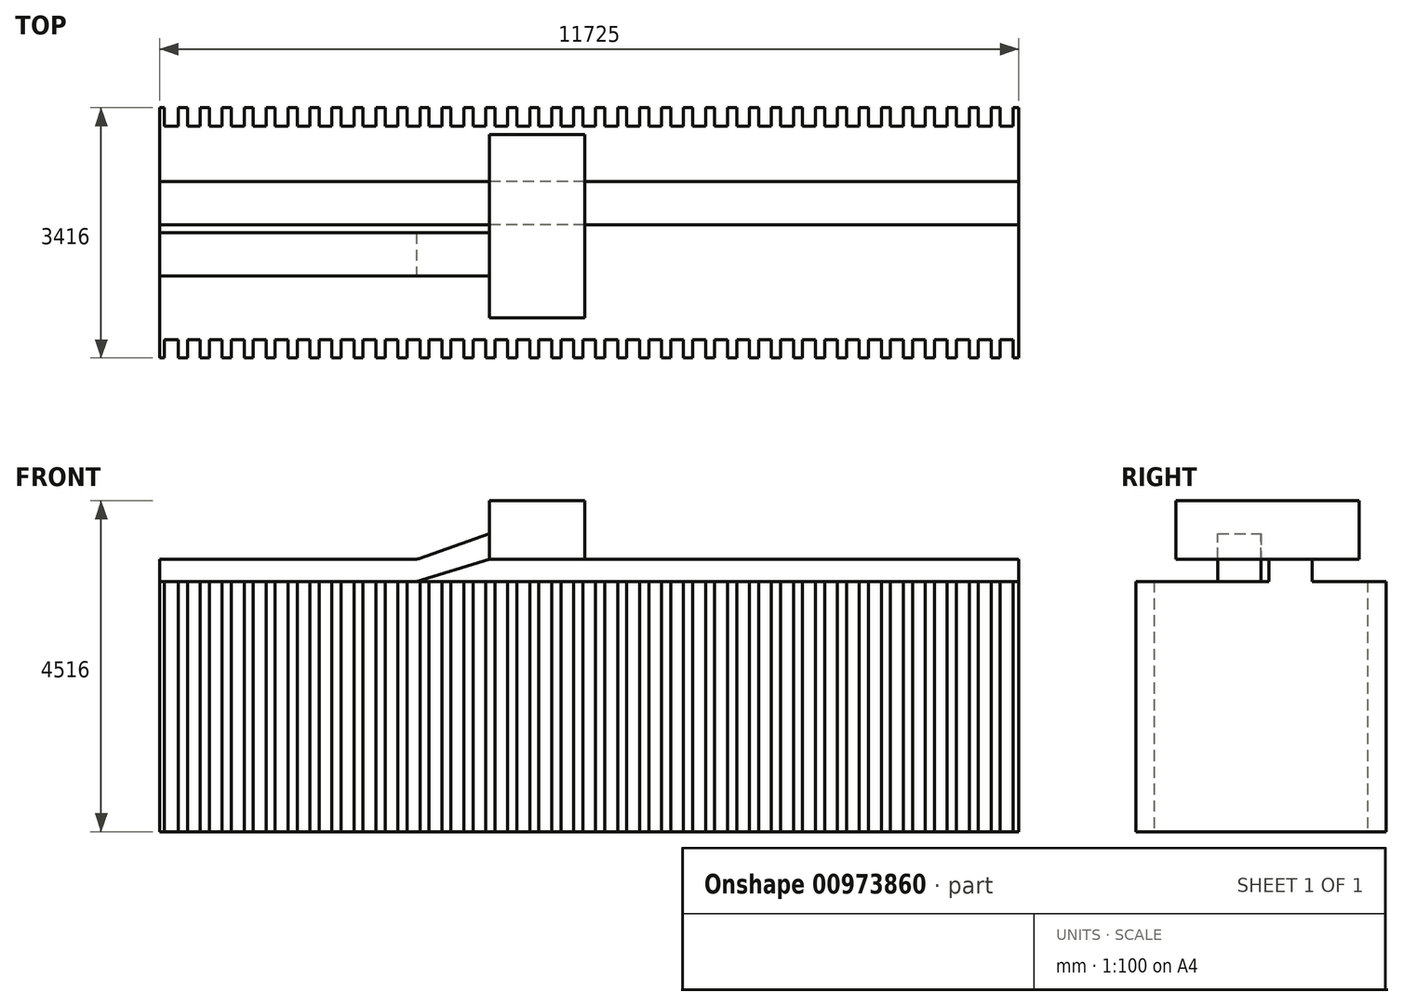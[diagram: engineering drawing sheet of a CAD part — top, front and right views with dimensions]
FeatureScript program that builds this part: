
annotation { "Feature Type Name" : "Feature", "Feature Type Description" : "" }
export const myFeature = defineFeature(function(context is Context, id is Id, definition is map)
    precondition{}
    {
        {
            var Q0;
            Q0=qCreatedBy(makeId("Top.planeOp"),FACE);
            var sketch = newSketch(context, id + "F0", { "sketchPlane" : qUnion([Q0])});
            skLineSegment(sketch, "E0.bottom", {"start": v(-25000, 7300) * mm, "end": v(25000, 7300) * mm});
            skLineSegment(sketch, "E0.top", {"start": v(-25000, -7300) * mm, "end": v(25000, -7300) * mm});
            skLineSegment(sketch, "E0.left", {"start": v(-25000, 7300) * mm, "end": v(-25000, -7300) * mm});
            skLineSegment(sketch, "E0.right", {"start": v(25000, 7300) * mm, "end": v(25000, -7300) * mm});
            skPoint(sketch, "E0.middle", {"position": v(0, 0) * mm});
            skSolve(sketch);
        }
        {
            var Q0;
            Q0=makeQuery(id+"F0.imprint","IMPRINT",FACE,{"disambiguationData":[TD([[makeQuery(id+"F0.imprint","IMPRINT",EDGE,{"derivedFrom":sQuery(id+"F0.wireOp",EDGE,"E0.bottom")}),-1.0]])]});
            var sketch = newSketch(context, id + "F1", { "sketchPlane" : qUnion([Q0])});
            skLineSegment(sketch, "E1", {"start": v(-20201.46, 5909) * mm, "end": v(-20138.96, 5909) * mm});
            skLineSegment(sketch, "E2", {"start": v(-20201.46, 5909) * mm, "end": v(-20201.46, 2493) * mm});
            skLineSegment(sketch, "E3", {"start": v(-20201.46, 2493) * mm, "end": v(-20138.96, 2493) * mm});
            skLineSegment(sketch, "E4", {"start": v(-8476.46, 2493) * mm, "end": v(-8476.46, 5909) * mm});
            skLineSegment(sketch, "E5.0", {"start": v(-20138.96, 5909) * mm, "end": v(-20138.96, 2493) * mm});
            skLineSegment(sketch, "E6.0", {"start": v(-19951.46, 5909) * mm, "end": v(-19951.46, 2493) * mm});
            skLineSegment(sketch, "E7.0", {"start": v(-19651.46, 5909) * mm, "end": v(-19651.46, 2493) * mm});
            skLineSegment(sketch, "E8.0", {"start": v(-19351.46, 5909) * mm, "end": v(-19351.46, 2493) * mm});
            skLineSegment(sketch, "E9.0", {"start": v(-19051.46, 5909) * mm, "end": v(-19051.46, 2493) * mm});
            skLineSegment(sketch, "E10.0", {"start": v(-18751.46, 5909) * mm, "end": v(-18751.46, 2493) * mm});
            skLineSegment(sketch, "E11.0", {"start": v(-18451.46, 5909) * mm, "end": v(-18451.46, 2493) * mm});
            skLineSegment(sketch, "E12.0", {"start": v(-18151.46, 5909) * mm, "end": v(-18151.46, 2493) * mm});
            skLineSegment(sketch, "E13.0", {"start": v(-17851.46, 5909) * mm, "end": v(-17851.46, 2493) * mm});
            skLineSegment(sketch, "E14.0", {"start": v(-17551.46, 5909) * mm, "end": v(-17551.46, 2493) * mm});
            skLineSegment(sketch, "E15.0", {"start": v(-17251.46, 5909) * mm, "end": v(-17251.46, 2493) * mm});
            skLineSegment(sketch, "E16.0", {"start": v(-16951.46, 5909) * mm, "end": v(-16951.46, 2493) * mm});
            skLineSegment(sketch, "E17.0", {"start": v(-16651.46, 5909) * mm, "end": v(-16651.46, 2493) * mm});
            skLineSegment(sketch, "E18.0", {"start": v(-16351.46, 5909) * mm, "end": v(-16351.46, 2493) * mm});
            skLineSegment(sketch, "E19.0", {"start": v(-16051.46, 5909) * mm, "end": v(-16051.46, 2493) * mm});
            skLineSegment(sketch, "E20.0", {"start": v(-15751.46, 5909) * mm, "end": v(-15751.46, 2493) * mm});
            skLineSegment(sketch, "E21.0", {"start": v(-25005, 7305) * mm, "end": v(-25005, -7305) * mm});
            skLineSegment(sketch, "E21.1", {"start": v(25005, 7305) * mm, "end": v(-25005, 7305) * mm});
            skLineSegment(sketch, "E21.2", {"start": v(25005, -7305) * mm, "end": v(25005, 7305) * mm});
            skLineSegment(sketch, "E21.3", {"start": v(-25005, -7305) * mm, "end": v(25005, -7305) * mm});
            skLineSegment(sketch, "E22.0", {"start": v(-15451.46, 5909) * mm, "end": v(-15451.46, 2493) * mm});
            skLineSegment(sketch, "E23.0", {"start": v(-15151.46, 5909) * mm, "end": v(-15151.46, 2493) * mm});
            skLineSegment(sketch, "E24.0", {"start": v(-14851.46, 5909) * mm, "end": v(-14851.46, 2493) * mm});
            skLineSegment(sketch, "E25.0", {"start": v(-14551.46, 5909) * mm, "end": v(-14551.46, 2493) * mm});
            skLineSegment(sketch, "E26.0", {"start": v(-14251.46, 5909) * mm, "end": v(-14251.46, 2493) * mm});
            skLineSegment(sketch, "E27.0", {"start": v(-13951.46, 5909) * mm, "end": v(-13951.46, 2493) * mm});
            skLineSegment(sketch, "E28.0", {"start": v(-13651.46, 5909) * mm, "end": v(-13651.46, 2493) * mm});
            skLineSegment(sketch, "E29.0", {"start": v(-13351.46, 5909) * mm, "end": v(-13351.46, 2493) * mm});
            skLineSegment(sketch, "E30.0", {"start": v(-13051.46, 5909) * mm, "end": v(-13051.46, 2493) * mm});
            skLineSegment(sketch, "E31.0", {"start": v(-12751.46, 5909) * mm, "end": v(-12751.46, 2493) * mm});
            skLineSegment(sketch, "E32.0", {"start": v(-12451.46, 5909) * mm, "end": v(-12451.46, 2493) * mm});
            skLineSegment(sketch, "E33.0", {"start": v(-12151.46, 5909) * mm, "end": v(-12151.46, 2493) * mm});
            skLineSegment(sketch, "E34.0", {"start": v(-11851.46, 5909) * mm, "end": v(-11851.46, 2493) * mm});
            skLineSegment(sketch, "E35.0", {"start": v(-11551.46, 5909) * mm, "end": v(-11551.46, 2493) * mm});
            skLineSegment(sketch, "E36.0", {"start": v(-11251.46, 5909) * mm, "end": v(-11251.46, 2493) * mm});
            skLineSegment(sketch, "E37.0", {"start": v(-10951.46, 5909) * mm, "end": v(-10951.46, 2493) * mm});
            skLineSegment(sketch, "E38.0", {"start": v(-10651.46, 5909) * mm, "end": v(-10651.46, 2493) * mm});
            skLineSegment(sketch, "E39.0", {"start": v(-10351.46, 5909) * mm, "end": v(-10351.46, 2493) * mm});
            skLineSegment(sketch, "E40.0", {"start": v(-10051.46, 5909) * mm, "end": v(-10051.46, 2493) * mm});
            skLineSegment(sketch, "E41.0", {"start": v(-9751.46, 5909) * mm, "end": v(-9751.46, 2493) * mm});
            skLineSegment(sketch, "E42.0", {"start": v(-9451.46, 5909) * mm, "end": v(-9451.46, 2493) * mm});
            skLineSegment(sketch, "E43.0", {"start": v(-9151.46, 5909) * mm, "end": v(-9151.46, 2493) * mm});
            skLineSegment(sketch, "E44.0", {"start": v(-8851.46, 5909) * mm, "end": v(-8851.46, 2493) * mm});
            skLineSegment(sketch, "E45.0", {"start": v(-8551.46, 5909) * mm, "end": v(-8551.46, 2493) * mm});
            skLineSegment(sketch, "E46.0", {"start": v(-19826.46, 5909) * mm, "end": v(-19826.46, 2493) * mm});
            skLineSegment(sketch, "E47.0", {"start": v(-19526.46, 5909) * mm, "end": v(-19526.46, 2493) * mm});
            skLineSegment(sketch, "E48.0", {"start": v(-19226.46, 5909) * mm, "end": v(-19226.46, 2493) * mm});
            skLineSegment(sketch, "E49.0", {"start": v(-18926.46, 5909) * mm, "end": v(-18926.46, 2493) * mm});
            skLineSegment(sketch, "E50.0", {"start": v(-18626.46, 5909) * mm, "end": v(-18626.46, 2493) * mm});
            skLineSegment(sketch, "E51.0", {"start": v(-18326.46, 5909) * mm, "end": v(-18326.46, 2493) * mm});
            skLineSegment(sketch, "E52.0", {"start": v(-18026.46, 5909) * mm, "end": v(-18026.46, 2493) * mm});
            skLineSegment(sketch, "E53.0", {"start": v(-17726.46, 5909) * mm, "end": v(-17726.46, 2493) * mm});
            skLineSegment(sketch, "E54.0", {"start": v(-17426.46, 5909) * mm, "end": v(-17426.46, 2493) * mm});
            skLineSegment(sketch, "E55.0", {"start": v(-17126.46, 5909) * mm, "end": v(-17126.46, 2493) * mm});
            skLineSegment(sketch, "E56.0", {"start": v(-16826.46, 5909) * mm, "end": v(-16826.46, 2493) * mm});
            skLineSegment(sketch, "E57.0", {"start": v(-16526.46, 5909) * mm, "end": v(-16526.46, 2493) * mm});
            skLineSegment(sketch, "E58.0", {"start": v(-16226.46, 5909) * mm, "end": v(-16226.46, 2493) * mm});
            skLineSegment(sketch, "E59.0", {"start": v(-15926.46, 5909) * mm, "end": v(-15926.46, 2493) * mm});
            skLineSegment(sketch, "E60.0", {"start": v(-15626.46, 5909) * mm, "end": v(-15626.46, 2493) * mm});
            skLineSegment(sketch, "E61.0", {"start": v(-15326.46, 5909) * mm, "end": v(-15326.46, 2493) * mm});
            skLineSegment(sketch, "E62.0", {"start": v(-15026.46, 5909) * mm, "end": v(-15026.46, 2493) * mm});
            skLineSegment(sketch, "E63.0", {"start": v(-14726.46, 5909) * mm, "end": v(-14726.46, 2493) * mm});
            skLineSegment(sketch, "E64.0", {"start": v(-14426.46, 5909) * mm, "end": v(-14426.46, 2493) * mm});
            skLineSegment(sketch, "E65.0", {"start": v(-14126.46, 5909) * mm, "end": v(-14126.46, 2493) * mm});
            skLineSegment(sketch, "E66.0", {"start": v(-13826.46, 5909) * mm, "end": v(-13826.46, 2493) * mm});
            skLineSegment(sketch, "E67.0", {"start": v(-13526.46, 5909) * mm, "end": v(-13526.46, 2493) * mm});
            skLineSegment(sketch, "E68.0", {"start": v(-13226.46, 5909) * mm, "end": v(-13226.46, 2493) * mm});
            skLineSegment(sketch, "E69.0", {"start": v(-12926.46, 5909) * mm, "end": v(-12926.46, 2493) * mm});
            skLineSegment(sketch, "E70.0", {"start": v(-12626.46, 5909) * mm, "end": v(-12626.46, 2493) * mm});
            skLineSegment(sketch, "E71.0", {"start": v(-12326.46, 5909) * mm, "end": v(-12326.46, 2493) * mm});
            skLineSegment(sketch, "E72.0", {"start": v(-12026.46, 5909) * mm, "end": v(-12026.46, 2493) * mm});
            skLineSegment(sketch, "E73.0", {"start": v(-11726.46, 5909) * mm, "end": v(-11726.46, 2493) * mm});
            skLineSegment(sketch, "E74.0", {"start": v(-11426.46, 5909) * mm, "end": v(-11426.46, 2493) * mm});
            skLineSegment(sketch, "E75.0", {"start": v(-11126.46, 5909) * mm, "end": v(-11126.46, 2493) * mm});
            skLineSegment(sketch, "E76.0", {"start": v(-10826.46, 5909) * mm, "end": v(-10826.46, 2493) * mm});
            skLineSegment(sketch, "E77.0", {"start": v(-10526.46, 5909) * mm, "end": v(-10526.46, 2493) * mm});
            skLineSegment(sketch, "E78.0", {"start": v(-10226.46, 5909) * mm, "end": v(-10226.46, 2493) * mm});
            skLineSegment(sketch, "E79.0", {"start": v(-9926.46, 5909) * mm, "end": v(-9926.46, 2493) * mm});
            skLineSegment(sketch, "E80.0", {"start": v(-9626.46, 5909) * mm, "end": v(-9626.46, 2493) * mm});
            skLineSegment(sketch, "E81.0", {"start": v(-9326.46, 5909) * mm, "end": v(-9326.46, 2493) * mm});
            skLineSegment(sketch, "E82.0", {"start": v(-9026.46, 5909) * mm, "end": v(-9026.46, 2493) * mm});
            skLineSegment(sketch, "E83.0", {"start": v(-8726.46, 5909) * mm, "end": v(-8726.46, 2493) * mm});
            skLineSegment(sketch, "E84", {"start": v(-20201.46, 5659) * mm, "end": v(-8476.46, 5659) * mm});
            skLineSegment(sketch, "E85", {"start": v(-20201.46, 2743) * mm, "end": v(-8476.46, 2743) * mm});
            skLineSegment(sketch, "E86.trimOffspring", {"start": v(-8551.46, 5909) * mm, "end": v(-8476.46, 5909) * mm});
            skLineSegment(sketch, "E87.trimOffspring", {"start": v(-8851.46, 5909) * mm, "end": v(-8726.46, 5909) * mm});
            skLineSegment(sketch, "E88.trimOffspring", {"start": v(-9151.46, 5909) * mm, "end": v(-9026.46, 5909) * mm});
            skLineSegment(sketch, "E89.trimOffspring", {"start": v(-9451.46, 5909) * mm, "end": v(-9326.46, 5909) * mm});
            skLineSegment(sketch, "E90.trimOffspring", {"start": v(-9751.46, 5909) * mm, "end": v(-9626.46, 5909) * mm});
            skLineSegment(sketch, "E91.trimOffspring", {"start": v(-10051.46, 5909) * mm, "end": v(-9926.46, 5909) * mm});
            skLineSegment(sketch, "E92.trimOffspring", {"start": v(-10351.46, 5909) * mm, "end": v(-10226.46, 5909) * mm});
            skLineSegment(sketch, "E93.trimOffspring", {"start": v(-10651.46, 5909) * mm, "end": v(-10526.46, 5909) * mm});
            skLineSegment(sketch, "E94.trimOffspring", {"start": v(-10951.46, 5909) * mm, "end": v(-10826.46, 5909) * mm});
            skLineSegment(sketch, "E95.trimOffspring", {"start": v(-11251.46, 5909) * mm, "end": v(-11126.46, 5909) * mm});
            skLineSegment(sketch, "E96.trimOffspring", {"start": v(-11551.46, 5909) * mm, "end": v(-11426.46, 5909) * mm});
            skLineSegment(sketch, "E97.trimOffspring", {"start": v(-11851.46, 5909) * mm, "end": v(-11726.46, 5909) * mm});
            skLineSegment(sketch, "E98.trimOffspring", {"start": v(-12151.46, 5909) * mm, "end": v(-12026.46, 5909) * mm});
            skLineSegment(sketch, "E99.trimOffspring", {"start": v(-12451.46, 5909) * mm, "end": v(-12326.46, 5909) * mm});
            skLineSegment(sketch, "E100.trimOffspring", {"start": v(-12751.46, 5909) * mm, "end": v(-12626.46, 5909) * mm});
            skLineSegment(sketch, "E101.trimOffspring", {"start": v(-13051.46, 5909) * mm, "end": v(-12926.46, 5909) * mm});
            skLineSegment(sketch, "E102.trimOffspring", {"start": v(-13351.46, 5909) * mm, "end": v(-13226.46, 5909) * mm});
            skLineSegment(sketch, "E103.trimOffspring", {"start": v(-13651.46, 5909) * mm, "end": v(-13526.46, 5909) * mm});
            skLineSegment(sketch, "E104.trimOffspring", {"start": v(-13951.46, 5909) * mm, "end": v(-13826.46, 5909) * mm});
            skLineSegment(sketch, "E105.trimOffspring", {"start": v(-14251.46, 5909) * mm, "end": v(-14126.46, 5909) * mm});
            skLineSegment(sketch, "E106.trimOffspring", {"start": v(-14551.46, 5909) * mm, "end": v(-14426.46, 5909) * mm});
            skLineSegment(sketch, "E107.trimOffspring", {"start": v(-14851.46, 5909) * mm, "end": v(-14726.46, 5909) * mm});
            skLineSegment(sketch, "E108.trimOffspring", {"start": v(-15151.46, 5909) * mm, "end": v(-15026.46, 5909) * mm});
            skLineSegment(sketch, "E109.trimOffspring", {"start": v(-15451.46, 5909) * mm, "end": v(-15326.46, 5909) * mm});
            skLineSegment(sketch, "E110.trimOffspring", {"start": v(-15751.46, 5909) * mm, "end": v(-15626.46, 5909) * mm});
            skLineSegment(sketch, "E111.trimOffspring", {"start": v(-16051.46, 5909) * mm, "end": v(-15926.46, 5909) * mm});
            skLineSegment(sketch, "E112.trimOffspring", {"start": v(-16351.46, 5909) * mm, "end": v(-16226.46, 5909) * mm});
            skLineSegment(sketch, "E113.trimOffspring", {"start": v(-16651.46, 5909) * mm, "end": v(-16526.46, 5909) * mm});
            skLineSegment(sketch, "E114.trimOffspring", {"start": v(-16951.46, 5909) * mm, "end": v(-16826.46, 5909) * mm});
            skLineSegment(sketch, "E115.trimOffspring", {"start": v(-17251.46, 5909) * mm, "end": v(-17126.46, 5909) * mm});
            skLineSegment(sketch, "E116.trimOffspring", {"start": v(-17551.46, 5909) * mm, "end": v(-17426.46, 5909) * mm});
            skLineSegment(sketch, "E117.trimOffspring", {"start": v(-17851.46, 5909) * mm, "end": v(-17726.46, 5909) * mm});
            skLineSegment(sketch, "E118.trimOffspring", {"start": v(-18151.46, 5909) * mm, "end": v(-18026.46, 5909) * mm});
            skLineSegment(sketch, "E119.trimOffspring", {"start": v(-18451.46, 5909) * mm, "end": v(-18326.46, 5909) * mm});
            skLineSegment(sketch, "E120.trimOffspring", {"start": v(-18751.46, 5909) * mm, "end": v(-18626.46, 5909) * mm});
            skLineSegment(sketch, "E121.trimOffspring", {"start": v(-19051.46, 5909) * mm, "end": v(-18926.46, 5909) * mm});
            skLineSegment(sketch, "E122.trimOffspring", {"start": v(-19351.46, 5909) * mm, "end": v(-19226.46, 5909) * mm});
            skLineSegment(sketch, "E123.trimOffspring", {"start": v(-19651.46, 5909) * mm, "end": v(-19526.46, 5909) * mm});
            skLineSegment(sketch, "E124.trimOffspring", {"start": v(-19951.46, 5909) * mm, "end": v(-19826.46, 5909) * mm});
            skLineSegment(sketch, "E125.trimOffspring", {"start": v(-19651.46, 2493) * mm, "end": v(-19526.46, 2493) * mm});
            skLineSegment(sketch, "E126.trimOffspring", {"start": v(-18751.46, 2493) * mm, "end": v(-18626.46, 2493) * mm});
            skLineSegment(sketch, "E127.trimOffspring", {"start": v(-17851.46, 2493) * mm, "end": v(-17726.46, 2493) * mm});
            skLineSegment(sketch, "E128.trimOffspring", {"start": v(-17251.46, 2493) * mm, "end": v(-17126.46, 2493) * mm});
            skLineSegment(sketch, "E129.trimOffspring", {"start": v(-16351.46, 2493) * mm, "end": v(-16226.46, 2493) * mm});
            skLineSegment(sketch, "E130.trimOffspring", {"start": v(-16951.46, 2493) * mm, "end": v(-16826.46, 2493) * mm});
            skLineSegment(sketch, "E131", {"start": v(-17551.46, 2493) * mm, "end": v(-17426.46, 2493) * mm});
            skLineSegment(sketch, "E132", {"start": v(-16651.46, 2493) * mm, "end": v(-16526.46, 2493) * mm});
            skLineSegment(sketch, "E133.trimOffspring", {"start": v(-15751.46, 2493) * mm, "end": v(-15626.46, 2493) * mm});
            skLineSegment(sketch, "E134.trimOffspring", {"start": v(-14551.46, 2493) * mm, "end": v(-14426.46, 2493) * mm});
            skLineSegment(sketch, "E135.trimOffspring", {"start": v(-15151.46, 2493) * mm, "end": v(-15026.46, 2493) * mm});
            skLineSegment(sketch, "E136.trimOffspring", {"start": v(-15451.46, 2493) * mm, "end": v(-15326.46, 2493) * mm});
            skLineSegment(sketch, "E137", {"start": v(-14851.46, 2493) * mm, "end": v(-14726.46, 2493) * mm});
            skLineSegment(sketch, "E138.trimOffspring", {"start": v(-13951.46, 2493) * mm, "end": v(-13826.46, 2493) * mm});
            skLineSegment(sketch, "E139.trimOffspring", {"start": v(-13351.46, 2493) * mm, "end": v(-13226.46, 2493) * mm});
            skLineSegment(sketch, "E140.trimOffspring", {"start": v(-13651.46, 2493) * mm, "end": v(-13526.46, 2493) * mm});
            skLineSegment(sketch, "E141", {"start": v(-14251.46, 2493) * mm, "end": v(-14126.46, 2493) * mm});
            skLineSegment(sketch, "E142.trimOffspring", {"start": v(-13051.46, 2493) * mm, "end": v(-12926.46, 2493) * mm});
            skLineSegment(sketch, "E143.trimOffspring", {"start": v(-12751.46, 2493) * mm, "end": v(-12626.46, 2493) * mm});
            skLineSegment(sketch, "E144.trimOffspring", {"start": v(-12151.46, 2493) * mm, "end": v(-12026.46, 2493) * mm});
            skLineSegment(sketch, "E145.trimOffspring", {"start": v(-11551.46, 2493) * mm, "end": v(-11426.46, 2493) * mm});
            skLineSegment(sketch, "E146.trimOffspring", {"start": v(-11851.46, 2493) * mm, "end": v(-11726.46, 2493) * mm});
            skLineSegment(sketch, "E147.trimOffspring", {"start": v(-11251.46, 2493) * mm, "end": v(-11126.46, 2493) * mm});
            skLineSegment(sketch, "E148.trimOffspring", {"start": v(-10951.46, 2493) * mm, "end": v(-10826.46, 2493) * mm});
            skLineSegment(sketch, "E149.trimOffspring", {"start": v(-10651.46, 2493) * mm, "end": v(-10526.46, 2493) * mm});
            skLineSegment(sketch, "E150.trimOffspring", {"start": v(-9751.46, 2493) * mm, "end": v(-9626.46, 2493) * mm});
            skLineSegment(sketch, "E151.trimOffspring", {"start": v(-8851.46, 2493) * mm, "end": v(-8726.46, 2493) * mm});
            skLineSegment(sketch, "E152", {"start": v(-10351.46, 2493) * mm, "end": v(-10226.46, 2493) * mm});
            skLineSegment(sketch, "E153", {"start": v(-10051.46, 2493) * mm, "end": v(-9926.46, 2493) * mm});
            skLineSegment(sketch, "E154", {"start": v(-9151.46, 2493) * mm, "end": v(-9026.46, 2493) * mm});
            skLineSegment(sketch, "E155.trimOffspring", {"start": v(-9451.46, 2493) * mm, "end": v(-9326.46, 2493) * mm});
            skLineSegment(sketch, "E156.trimOffspring", {"start": v(-8551.46, 2493) * mm, "end": v(-8476.46, 2493) * mm});
            skLineSegment(sketch, "E157.trimOffspring", {"start": v(-18451.46, 2493) * mm, "end": v(-18326.46, 2493) * mm});
            skLineSegment(sketch, "E158.trimOffspring", {"start": v(-19351.46, 2493) * mm, "end": v(-19226.46, 2493) * mm});
            skLineSegment(sketch, "E159", {"start": v(-19051.46, 2493) * mm, "end": v(-18926.46, 2493) * mm});
            skLineSegment(sketch, "E160", {"start": v(-18151.46, 2493) * mm, "end": v(-18026.46, 2493) * mm});
            skLineSegment(sketch, "E161", {"start": v(-16051.46, 2493) * mm, "end": v(-15926.46, 2493) * mm});
            skLineSegment(sketch, "E162", {"start": v(-19951.46, 2493) * mm, "end": v(-19826.46, 2493) * mm});
            skLineSegment(sketch, "E163", {"start": v(-12451.46, 2493) * mm, "end": v(-12326.46, 2493) * mm});
            skSolve(sketch);
        }
        {
            var Q0;
            {var subQ0=sQuery(id+"F1.wireOp",EDGE,"E88.trimOffspring");Q0=makeQuery(id+"F1.imprint","IMPRINT",FACE,{"disambiguationData":[TD([[makeQuery(id+"F1.imprint","IMPRINT",EDGE,{"derivedFrom":subQ0}),-1.0]])]});}
            var Q1;
            {var subQ0=sQuery(id+"F1.wireOp",EDGE,"E112.trimOffspring");Q1=makeQuery(id+"F1.imprint","IMPRINT",FACE,{"disambiguationData":[TD([[makeQuery(id+"F1.imprint","IMPRINT",EDGE,{"derivedFrom":subQ0}),-1.0]])]});}
            var Q2;
            {var subQ0=sQuery(id+"F1.wireOp",EDGE,"E84");var subQ1=sQuery(id+"F1.wireOp",EDGE,"E38.0");var subQ2=makeQuery(id+"F1.imprint","INTERSECT",VERTEX,{"derivedFrom":[subQ1,subQ0]});Q2=makeQuery(id+"F1.imprint","IMPRINT",FACE,{"disambiguationData":[TD([[makeQuery(id+"F1.imprint","IMPRINT",EDGE,{"disambiguationData":[TD([[subQ2,-1.0]])],"derivedFrom":subQ1}),1.0]])]});}
            var Q3;
            {var subQ0=sQuery(id+"F1.wireOp",EDGE,"E158.trimOffspring");Q3=makeQuery(id+"F1.imprint","IMPRINT",FACE,{"disambiguationData":[TD([[makeQuery(id+"F1.imprint","IMPRINT",EDGE,{"derivedFrom":subQ0}),1.0]])]});}
            var Q4;
            {var subQ0=sQuery(id+"F1.wireOp",EDGE,"E84");var subQ1=sQuery(id+"F1.wireOp",EDGE,"E18.0");var subQ2=makeQuery(id+"F1.imprint","INTERSECT",VERTEX,{"derivedFrom":[subQ1,subQ0]});Q4=makeQuery(id+"F1.imprint","IMPRINT",FACE,{"disambiguationData":[TD([[makeQuery(id+"F1.imprint","IMPRINT",EDGE,{"disambiguationData":[TD([[subQ2,-1.0]])],"derivedFrom":subQ1}),-1.0]])]});}
            var Q5;
            {var subQ0=sQuery(id+"F1.wireOp",EDGE,"E140.trimOffspring");Q5=makeQuery(id+"F1.imprint","IMPRINT",FACE,{"disambiguationData":[TD([[makeQuery(id+"F1.imprint","IMPRINT",EDGE,{"derivedFrom":subQ0}),1.0]])]});}
            var Q6;
            {var subQ0=sQuery(id+"F1.wireOp",EDGE,"E84");var subQ1=sQuery(id+"F1.wireOp",EDGE,"E35.0");var subQ2=makeQuery(id+"F1.imprint","INTERSECT",VERTEX,{"derivedFrom":[subQ1,subQ0]});Q6=makeQuery(id+"F1.imprint","IMPRINT",FACE,{"disambiguationData":[TD([[makeQuery(id+"F1.imprint","IMPRINT",EDGE,{"disambiguationData":[TD([[subQ2,-1.0]])],"derivedFrom":subQ1}),-1.0]])]});}
            var Q7;
            {var subQ0=sQuery(id+"F1.wireOp",EDGE,"E107.trimOffspring");Q7=makeQuery(id+"F1.imprint","IMPRINT",FACE,{"disambiguationData":[TD([[makeQuery(id+"F1.imprint","IMPRINT",EDGE,{"derivedFrom":subQ0}),-1.0]])]});}
            var Q8;
            {var subQ0=sQuery(id+"F1.wireOp",EDGE,"E129.trimOffspring");Q8=makeQuery(id+"F1.imprint","IMPRINT",FACE,{"disambiguationData":[TD([[makeQuery(id+"F1.imprint","IMPRINT",EDGE,{"derivedFrom":subQ0}),1.0]])]});}
            var Q9;
            {var subQ0=sQuery(id+"F1.wireOp",EDGE,"E120.trimOffspring");Q9=makeQuery(id+"F1.imprint","IMPRINT",FACE,{"disambiguationData":[TD([[makeQuery(id+"F1.imprint","IMPRINT",EDGE,{"derivedFrom":subQ0}),-1.0]])]});}
            var Q10;
            {var subQ0=sQuery(id+"F1.wireOp",EDGE,"E115.trimOffspring");Q10=makeQuery(id+"F1.imprint","IMPRINT",FACE,{"disambiguationData":[TD([[makeQuery(id+"F1.imprint","IMPRINT",EDGE,{"derivedFrom":subQ0}),-1.0]])]});}
            var Q11;
            {var subQ0=sQuery(id+"F1.wireOp",EDGE,"E138.trimOffspring");Q11=makeQuery(id+"F1.imprint","IMPRINT",FACE,{"disambiguationData":[TD([[makeQuery(id+"F1.imprint","IMPRINT",EDGE,{"derivedFrom":subQ0}),1.0]])]});}
            var Q12;
            {var subQ0=sQuery(id+"F1.wireOp",EDGE,"E84");var subQ1=sQuery(id+"F1.wireOp",EDGE,"E11.0");var subQ2=makeQuery(id+"F1.imprint","INTERSECT",VERTEX,{"derivedFrom":[subQ1,subQ0]});Q12=makeQuery(id+"F1.imprint","IMPRINT",FACE,{"disambiguationData":[TD([[makeQuery(id+"F1.imprint","IMPRINT",EDGE,{"disambiguationData":[TD([[subQ2,-1.0]])],"derivedFrom":subQ1}),1.0]])]});}
            var Q13;
            {var subQ0=sQuery(id+"F1.wireOp",EDGE,"E91.trimOffspring");Q13=makeQuery(id+"F1.imprint","IMPRINT",FACE,{"disambiguationData":[TD([[makeQuery(id+"F1.imprint","IMPRINT",EDGE,{"derivedFrom":subQ0}),-1.0]])]});}
            var Q14;
            {var subQ0=sQuery(id+"F1.wireOp",EDGE,"E84");var subQ1=sQuery(id+"F1.wireOp",EDGE,"E13.0");var subQ2=makeQuery(id+"F1.imprint","INTERSECT",VERTEX,{"derivedFrom":[subQ1,subQ0]});Q14=makeQuery(id+"F1.imprint","IMPRINT",FACE,{"disambiguationData":[TD([[makeQuery(id+"F1.imprint","IMPRINT",EDGE,{"disambiguationData":[TD([[subQ2,-1.0]])],"derivedFrom":subQ1}),-1.0]])]});}
            var Q15;
            {var subQ0=sQuery(id+"F1.wireOp",EDGE,"E84");var subQ1=sQuery(id+"F1.wireOp",EDGE,"E26.0");var subQ2=makeQuery(id+"F1.imprint","INTERSECT",VERTEX,{"derivedFrom":[subQ1,subQ0]});Q15=makeQuery(id+"F1.imprint","IMPRINT",FACE,{"disambiguationData":[TD([[makeQuery(id+"F1.imprint","IMPRINT",EDGE,{"disambiguationData":[TD([[subQ2,-1.0]])],"derivedFrom":subQ1}),-1.0]])]});}
            var Q16;
            {var subQ0=sQuery(id+"F1.wireOp",EDGE,"E121.trimOffspring");Q16=makeQuery(id+"F1.imprint","IMPRINT",FACE,{"disambiguationData":[TD([[makeQuery(id+"F1.imprint","IMPRINT",EDGE,{"derivedFrom":subQ0}),-1.0]])]});}
            var Q17;
            {var subQ0=sQuery(id+"F1.wireOp",EDGE,"E130.trimOffspring");Q17=makeQuery(id+"F1.imprint","IMPRINT",FACE,{"disambiguationData":[TD([[makeQuery(id+"F1.imprint","IMPRINT",EDGE,{"derivedFrom":subQ0}),1.0]])]});}
            var Q18;
            {var subQ0=sQuery(id+"F1.wireOp",EDGE,"E154");Q18=makeQuery(id+"F1.imprint","IMPRINT",FACE,{"disambiguationData":[TD([[makeQuery(id+"F1.imprint","IMPRINT",EDGE,{"derivedFrom":subQ0}),1.0]])]});}
            var Q19;
            {var subQ0=sQuery(id+"F1.wireOp",EDGE,"E151.trimOffspring");Q19=makeQuery(id+"F1.imprint","IMPRINT",FACE,{"disambiguationData":[TD([[makeQuery(id+"F1.imprint","IMPRINT",EDGE,{"derivedFrom":subQ0}),1.0]])]});}
            var Q20;
            {var subQ0=sQuery(id+"F1.wireOp",EDGE,"E84");var subQ1=sQuery(id+"F1.wireOp",EDGE,"E30.0");var subQ2=makeQuery(id+"F1.imprint","INTERSECT",VERTEX,{"derivedFrom":[subQ1,subQ0]});Q20=makeQuery(id+"F1.imprint","IMPRINT",FACE,{"disambiguationData":[TD([[makeQuery(id+"F1.imprint","IMPRINT",EDGE,{"disambiguationData":[TD([[subQ2,-1.0]])],"derivedFrom":subQ1}),-1.0]])]});}
            var Q21;
            {var subQ0=sQuery(id+"F1.wireOp",EDGE,"E84");var subQ1=sQuery(id+"F1.wireOp",EDGE,"E19.0");var subQ2=makeQuery(id+"F1.imprint","INTERSECT",VERTEX,{"derivedFrom":[subQ1,subQ0]});Q21=makeQuery(id+"F1.imprint","IMPRINT",FACE,{"disambiguationData":[TD([[makeQuery(id+"F1.imprint","IMPRINT",EDGE,{"disambiguationData":[TD([[subQ2,-1.0]])],"derivedFrom":subQ1}),1.0]])]});}
            var Q22;
            {var subQ0=sQuery(id+"F1.wireOp",EDGE,"E84");var subQ1=sQuery(id+"F1.wireOp",EDGE,"E14.0");var subQ2=makeQuery(id+"F1.imprint","INTERSECT",VERTEX,{"derivedFrom":[subQ1,subQ0]});Q22=makeQuery(id+"F1.imprint","IMPRINT",FACE,{"disambiguationData":[TD([[makeQuery(id+"F1.imprint","IMPRINT",EDGE,{"disambiguationData":[TD([[subQ2,-1.0]])],"derivedFrom":subQ1}),-1.0]])]});}
            var Q23;
            {var subQ0=sQuery(id+"F1.wireOp",EDGE,"E84");var subQ1=sQuery(id+"F1.wireOp",EDGE,"E12.0");var subQ2=makeQuery(id+"F1.imprint","INTERSECT",VERTEX,{"derivedFrom":[subQ1,subQ0]});Q23=makeQuery(id+"F1.imprint","IMPRINT",FACE,{"disambiguationData":[TD([[makeQuery(id+"F1.imprint","IMPRINT",EDGE,{"disambiguationData":[TD([[subQ2,-1.0]])],"derivedFrom":subQ1}),1.0]])]});}
            var Q24;
            {var subQ0=sQuery(id+"F1.wireOp",EDGE,"E143.trimOffspring");Q24=makeQuery(id+"F1.imprint","IMPRINT",FACE,{"disambiguationData":[TD([[makeQuery(id+"F1.imprint","IMPRINT",EDGE,{"derivedFrom":subQ0}),1.0]])]});}
            var Q25;
            {var subQ0=sQuery(id+"F1.wireOp",EDGE,"E161");Q25=makeQuery(id+"F1.imprint","IMPRINT",FACE,{"disambiguationData":[TD([[makeQuery(id+"F1.imprint","IMPRINT",EDGE,{"derivedFrom":subQ0}),1.0]])]});}
            var Q26;
            {var subQ0=sQuery(id+"F1.wireOp",EDGE,"E100.trimOffspring");Q26=makeQuery(id+"F1.imprint","IMPRINT",FACE,{"disambiguationData":[TD([[makeQuery(id+"F1.imprint","IMPRINT",EDGE,{"derivedFrom":subQ0}),-1.0]])]});}
            var Q27;
            {var subQ0=sQuery(id+"F1.wireOp",EDGE,"E84");var subQ1=sQuery(id+"F1.wireOp",EDGE,"E15.0");var subQ2=makeQuery(id+"F1.imprint","INTERSECT",VERTEX,{"derivedFrom":[subQ1,subQ0]});Q27=makeQuery(id+"F1.imprint","IMPRINT",FACE,{"disambiguationData":[TD([[makeQuery(id+"F1.imprint","IMPRINT",EDGE,{"disambiguationData":[TD([[subQ2,-1.0]])],"derivedFrom":subQ1}),-1.0]])]});}
            var Q28;
            {var subQ0=sQuery(id+"F1.wireOp",EDGE,"E84");var subQ1=sQuery(id+"F1.wireOp",EDGE,"E39.0");var subQ2=makeQuery(id+"F1.imprint","INTERSECT",VERTEX,{"derivedFrom":[subQ1,subQ0]});Q28=makeQuery(id+"F1.imprint","IMPRINT",FACE,{"disambiguationData":[TD([[makeQuery(id+"F1.imprint","IMPRINT",EDGE,{"disambiguationData":[TD([[subQ2,-1.0]])],"derivedFrom":subQ1}),1.0]])]});}
            var Q29;
            {var subQ0=sQuery(id+"F1.wireOp",EDGE,"E84");var subQ1=sQuery(id+"F1.wireOp",EDGE,"E36.0");var subQ2=makeQuery(id+"F1.imprint","INTERSECT",VERTEX,{"derivedFrom":[subQ1,subQ0]});Q29=makeQuery(id+"F1.imprint","IMPRINT",FACE,{"disambiguationData":[TD([[makeQuery(id+"F1.imprint","IMPRINT",EDGE,{"disambiguationData":[TD([[subQ2,-1.0]])],"derivedFrom":subQ1}),1.0]])]});}
            var Q30;
            {var subQ0=sQuery(id+"F1.wireOp",EDGE,"E84");var subQ1=sQuery(id+"F1.wireOp",EDGE,"E40.0");var subQ2=makeQuery(id+"F1.imprint","INTERSECT",VERTEX,{"derivedFrom":[subQ1,subQ0]});Q30=makeQuery(id+"F1.imprint","IMPRINT",FACE,{"disambiguationData":[TD([[makeQuery(id+"F1.imprint","IMPRINT",EDGE,{"disambiguationData":[TD([[subQ2,-1.0]])],"derivedFrom":subQ1}),1.0]])]});}
            var Q31;
            {var subQ0=sQuery(id+"F1.wireOp",EDGE,"E118.trimOffspring");Q31=makeQuery(id+"F1.imprint","IMPRINT",FACE,{"disambiguationData":[TD([[makeQuery(id+"F1.imprint","IMPRINT",EDGE,{"derivedFrom":subQ0}),-1.0]])]});}
            var Q32;
            {var subQ0=sQuery(id+"F1.wireOp",EDGE,"E84");var subQ1=sQuery(id+"F1.wireOp",EDGE,"E10.0");var subQ2=makeQuery(id+"F1.imprint","INTERSECT",VERTEX,{"derivedFrom":[subQ1,subQ0]});Q32=makeQuery(id+"F1.imprint","IMPRINT",FACE,{"disambiguationData":[TD([[makeQuery(id+"F1.imprint","IMPRINT",EDGE,{"disambiguationData":[TD([[subQ2,-1.0]])],"derivedFrom":subQ1}),-1.0]])]});}
            var Q33;
            {var subQ0=sQuery(id+"F1.wireOp",EDGE,"E84");var subQ1=sQuery(id+"F1.wireOp",EDGE,"E19.0");var subQ2=makeQuery(id+"F1.imprint","INTERSECT",VERTEX,{"derivedFrom":[subQ1,subQ0]});Q33=makeQuery(id+"F1.imprint","IMPRINT",FACE,{"disambiguationData":[TD([[makeQuery(id+"F1.imprint","IMPRINT",EDGE,{"disambiguationData":[TD([[subQ2,-1.0]])],"derivedFrom":subQ1}),-1.0]])]});}
            var Q34;
            {var subQ0=sQuery(id+"F1.wireOp",EDGE,"E84");var subQ1=sQuery(id+"F1.wireOp",EDGE,"E29.0");var subQ2=makeQuery(id+"F1.imprint","INTERSECT",VERTEX,{"derivedFrom":[subQ1,subQ0]});Q34=makeQuery(id+"F1.imprint","IMPRINT",FACE,{"disambiguationData":[TD([[makeQuery(id+"F1.imprint","IMPRINT",EDGE,{"disambiguationData":[TD([[subQ2,-1.0]])],"derivedFrom":subQ1}),-1.0]])]});}
            var Q35;
            {var subQ0=sQuery(id+"F1.wireOp",EDGE,"E84");var subQ1=sQuery(id+"F1.wireOp",EDGE,"E9.0");var subQ2=makeQuery(id+"F1.imprint","INTERSECT",VERTEX,{"derivedFrom":[subQ1,subQ0]});Q35=makeQuery(id+"F1.imprint","IMPRINT",FACE,{"disambiguationData":[TD([[makeQuery(id+"F1.imprint","IMPRINT",EDGE,{"disambiguationData":[TD([[subQ2,-1.0]])],"derivedFrom":subQ1}),-1.0]])]});}
            var Q36;
            {var subQ0=sQuery(id+"F1.wireOp",EDGE,"E102.trimOffspring");Q36=makeQuery(id+"F1.imprint","IMPRINT",FACE,{"disambiguationData":[TD([[makeQuery(id+"F1.imprint","IMPRINT",EDGE,{"derivedFrom":subQ0}),-1.0]])]});}
            var Q37;
            {var subQ0=sQuery(id+"F1.wireOp",EDGE,"E99.trimOffspring");Q37=makeQuery(id+"F1.imprint","IMPRINT",FACE,{"disambiguationData":[TD([[makeQuery(id+"F1.imprint","IMPRINT",EDGE,{"derivedFrom":subQ0}),-1.0]])]});}
            var Q38;
            {var subQ0=sQuery(id+"F1.wireOp",EDGE,"E117.trimOffspring");Q38=makeQuery(id+"F1.imprint","IMPRINT",FACE,{"disambiguationData":[TD([[makeQuery(id+"F1.imprint","IMPRINT",EDGE,{"derivedFrom":subQ0}),-1.0]])]});}
            var Q39;
            {var subQ0=sQuery(id+"F1.wireOp",EDGE,"E84");var subQ1=sQuery(id+"F1.wireOp",EDGE,"E17.0");var subQ2=makeQuery(id+"F1.imprint","INTERSECT",VERTEX,{"derivedFrom":[subQ1,subQ0]});Q39=makeQuery(id+"F1.imprint","IMPRINT",FACE,{"disambiguationData":[TD([[makeQuery(id+"F1.imprint","IMPRINT",EDGE,{"disambiguationData":[TD([[subQ2,-1.0]])],"derivedFrom":subQ1}),-1.0]])]});}
            var Q40;
            {var subQ0=sQuery(id+"F1.wireOp",EDGE,"E84");var subQ1=sQuery(id+"F1.wireOp",EDGE,"E33.0");var subQ2=makeQuery(id+"F1.imprint","INTERSECT",VERTEX,{"derivedFrom":[subQ1,subQ0]});Q40=makeQuery(id+"F1.imprint","IMPRINT",FACE,{"disambiguationData":[TD([[makeQuery(id+"F1.imprint","IMPRINT",EDGE,{"disambiguationData":[TD([[subQ2,-1.0]])],"derivedFrom":subQ1}),-1.0]])]});}
            var Q41;
            {var subQ0=sQuery(id+"F1.wireOp",EDGE,"E146.trimOffspring");Q41=makeQuery(id+"F1.imprint","IMPRINT",FACE,{"disambiguationData":[TD([[makeQuery(id+"F1.imprint","IMPRINT",EDGE,{"derivedFrom":subQ0}),1.0]])]});}
            var Q42;
            {var subQ0=sQuery(id+"F1.wireOp",EDGE,"E95.trimOffspring");Q42=makeQuery(id+"F1.imprint","IMPRINT",FACE,{"disambiguationData":[TD([[makeQuery(id+"F1.imprint","IMPRINT",EDGE,{"derivedFrom":subQ0}),-1.0]])]});}
            var Q43;
            {var subQ0=sQuery(id+"F1.wireOp",EDGE,"E134.trimOffspring");Q43=makeQuery(id+"F1.imprint","IMPRINT",FACE,{"disambiguationData":[TD([[makeQuery(id+"F1.imprint","IMPRINT",EDGE,{"derivedFrom":subQ0}),1.0]])]});}
            var Q44;
            {var subQ0=sQuery(id+"F1.wireOp",EDGE,"E122.trimOffspring");Q44=makeQuery(id+"F1.imprint","IMPRINT",FACE,{"disambiguationData":[TD([[makeQuery(id+"F1.imprint","IMPRINT",EDGE,{"derivedFrom":subQ0}),-1.0]])]});}
            var Q45;
            {var subQ0=sQuery(id+"F1.wireOp",EDGE,"E105.trimOffspring");Q45=makeQuery(id+"F1.imprint","IMPRINT",FACE,{"disambiguationData":[TD([[makeQuery(id+"F1.imprint","IMPRINT",EDGE,{"derivedFrom":subQ0}),-1.0]])]});}
            var Q46;
            {var subQ0=sQuery(id+"F1.wireOp",EDGE,"E84");var subQ1=sQuery(id+"F1.wireOp",EDGE,"E31.0");var subQ2=makeQuery(id+"F1.imprint","INTERSECT",VERTEX,{"derivedFrom":[subQ1,subQ0]});Q46=makeQuery(id+"F1.imprint","IMPRINT",FACE,{"disambiguationData":[TD([[makeQuery(id+"F1.imprint","IMPRINT",EDGE,{"disambiguationData":[TD([[subQ2,-1.0]])],"derivedFrom":subQ1}),-1.0]])]});}
            var Q47;
            {var subQ0=sQuery(id+"F1.wireOp",EDGE,"E84");var subQ1=sQuery(id+"F1.wireOp",EDGE,"E24.0");var subQ2=makeQuery(id+"F1.imprint","INTERSECT",VERTEX,{"derivedFrom":[subQ1,subQ0]});Q47=makeQuery(id+"F1.imprint","IMPRINT",FACE,{"disambiguationData":[TD([[makeQuery(id+"F1.imprint","IMPRINT",EDGE,{"disambiguationData":[TD([[subQ2,-1.0]])],"derivedFrom":subQ1}),1.0]])]});}
            var Q48;
            {var subQ0=sQuery(id+"F1.wireOp",EDGE,"E84");var subQ1=sQuery(id+"F1.wireOp",EDGE,"E43.0");var subQ2=makeQuery(id+"F1.imprint","INTERSECT",VERTEX,{"derivedFrom":[subQ1,subQ0]});Q48=makeQuery(id+"F1.imprint","IMPRINT",FACE,{"disambiguationData":[TD([[makeQuery(id+"F1.imprint","IMPRINT",EDGE,{"disambiguationData":[TD([[subQ2,-1.0]])],"derivedFrom":subQ1}),1.0]])]});}
            var Q49;
            {var subQ0=sQuery(id+"F1.wireOp",EDGE,"E123.trimOffspring");Q49=makeQuery(id+"F1.imprint","IMPRINT",FACE,{"disambiguationData":[TD([[makeQuery(id+"F1.imprint","IMPRINT",EDGE,{"derivedFrom":subQ0}),-1.0]])]});}
            var Q50;
            {var subQ0=sQuery(id+"F1.wireOp",EDGE,"E84");var subQ1=sQuery(id+"F1.wireOp",EDGE,"E43.0");var subQ2=makeQuery(id+"F1.imprint","INTERSECT",VERTEX,{"derivedFrom":[subQ1,subQ0]});Q50=makeQuery(id+"F1.imprint","IMPRINT",FACE,{"disambiguationData":[TD([[makeQuery(id+"F1.imprint","IMPRINT",EDGE,{"disambiguationData":[TD([[subQ2,-1.0]])],"derivedFrom":subQ1}),-1.0]])]});}
            var Q51;
            {var subQ0=sQuery(id+"F1.wireOp",EDGE,"E84");var subQ1=sQuery(id+"F1.wireOp",EDGE,"E32.0");var subQ2=makeQuery(id+"F1.imprint","INTERSECT",VERTEX,{"derivedFrom":[subQ1,subQ0]});Q51=makeQuery(id+"F1.imprint","IMPRINT",FACE,{"disambiguationData":[TD([[makeQuery(id+"F1.imprint","IMPRINT",EDGE,{"disambiguationData":[TD([[subQ2,-1.0]])],"derivedFrom":subQ1}),1.0]])]});}
            var Q52;
            {var subQ0=sQuery(id+"F1.wireOp",EDGE,"E133.trimOffspring");Q52=makeQuery(id+"F1.imprint","IMPRINT",FACE,{"disambiguationData":[TD([[makeQuery(id+"F1.imprint","IMPRINT",EDGE,{"derivedFrom":subQ0}),1.0]])]});}
            var Q53;
            {var subQ0=sQuery(id+"F1.wireOp",EDGE,"E84");var subQ1=sQuery(id+"F1.wireOp",EDGE,"E37.0");var subQ2=makeQuery(id+"F1.imprint","INTERSECT",VERTEX,{"derivedFrom":[subQ1,subQ0]});Q53=makeQuery(id+"F1.imprint","IMPRINT",FACE,{"disambiguationData":[TD([[makeQuery(id+"F1.imprint","IMPRINT",EDGE,{"disambiguationData":[TD([[subQ2,-1.0]])],"derivedFrom":subQ1}),1.0]])]});}
            var Q54;
            {var subQ0=sQuery(id+"F1.wireOp",EDGE,"E141");Q54=makeQuery(id+"F1.imprint","IMPRINT",FACE,{"disambiguationData":[TD([[makeQuery(id+"F1.imprint","IMPRINT",EDGE,{"derivedFrom":subQ0}),1.0]])]});}
            var Q55;
            {var subQ0=sQuery(id+"F1.wireOp",EDGE,"E84");var subQ1=sQuery(id+"F1.wireOp",EDGE,"E17.0");var subQ2=makeQuery(id+"F1.imprint","INTERSECT",VERTEX,{"derivedFrom":[subQ1,subQ0]});Q55=makeQuery(id+"F1.imprint","IMPRINT",FACE,{"disambiguationData":[TD([[makeQuery(id+"F1.imprint","IMPRINT",EDGE,{"disambiguationData":[TD([[subQ2,-1.0]])],"derivedFrom":subQ1}),1.0]])]});}
            var Q56;
            {var subQ0=sQuery(id+"F1.wireOp",EDGE,"E127.trimOffspring");Q56=makeQuery(id+"F1.imprint","IMPRINT",FACE,{"disambiguationData":[TD([[makeQuery(id+"F1.imprint","IMPRINT",EDGE,{"derivedFrom":subQ0}),1.0]])]});}
            var Q57;
            {var subQ0=sQuery(id+"F1.wireOp",EDGE,"E84");var subQ1=sQuery(id+"F1.wireOp",EDGE,"E8.0");var subQ2=makeQuery(id+"F1.imprint","INTERSECT",VERTEX,{"derivedFrom":[subQ1,subQ0]});Q57=makeQuery(id+"F1.imprint","IMPRINT",FACE,{"disambiguationData":[TD([[makeQuery(id+"F1.imprint","IMPRINT",EDGE,{"disambiguationData":[TD([[subQ2,-1.0]])],"derivedFrom":subQ1}),-1.0]])]});}
            var Q58;
            {var subQ0=sQuery(id+"F1.wireOp",EDGE,"E84");var subQ1=sQuery(id+"F1.wireOp",EDGE,"E35.0");var subQ2=makeQuery(id+"F1.imprint","INTERSECT",VERTEX,{"derivedFrom":[subQ1,subQ0]});Q58=makeQuery(id+"F1.imprint","IMPRINT",FACE,{"disambiguationData":[TD([[makeQuery(id+"F1.imprint","IMPRINT",EDGE,{"disambiguationData":[TD([[subQ2,-1.0]])],"derivedFrom":subQ1}),1.0]])]});}
            var Q59;
            {var subQ0=sQuery(id+"F1.wireOp",EDGE,"E84");var subQ1=sQuery(id+"F1.wireOp",EDGE,"E27.0");var subQ2=makeQuery(id+"F1.imprint","INTERSECT",VERTEX,{"derivedFrom":[subQ1,subQ0]});Q59=makeQuery(id+"F1.imprint","IMPRINT",FACE,{"disambiguationData":[TD([[makeQuery(id+"F1.imprint","IMPRINT",EDGE,{"disambiguationData":[TD([[subQ2,-1.0]])],"derivedFrom":subQ1}),1.0]])]});}
            var Q60;
            {var subQ0=sQuery(id+"F1.wireOp",EDGE,"E84");var subQ1=sQuery(id+"F1.wireOp",EDGE,"E42.0");var subQ2=makeQuery(id+"F1.imprint","INTERSECT",VERTEX,{"derivedFrom":[subQ1,subQ0]});Q60=makeQuery(id+"F1.imprint","IMPRINT",FACE,{"disambiguationData":[TD([[makeQuery(id+"F1.imprint","IMPRINT",EDGE,{"disambiguationData":[TD([[subQ2,-1.0]])],"derivedFrom":subQ1}),-1.0]])]});}
            var Q61;
            {var subQ0=sQuery(id+"F1.wireOp",EDGE,"E93.trimOffspring");Q61=makeQuery(id+"F1.imprint","IMPRINT",FACE,{"disambiguationData":[TD([[makeQuery(id+"F1.imprint","IMPRINT",EDGE,{"derivedFrom":subQ0}),-1.0]])]});}
            var Q62;
            {var subQ0=sQuery(id+"F1.wireOp",EDGE,"E84");var subQ1=sQuery(id+"F1.wireOp",EDGE,"E28.0");var subQ2=makeQuery(id+"F1.imprint","INTERSECT",VERTEX,{"derivedFrom":[subQ1,subQ0]});Q62=makeQuery(id+"F1.imprint","IMPRINT",FACE,{"disambiguationData":[TD([[makeQuery(id+"F1.imprint","IMPRINT",EDGE,{"disambiguationData":[TD([[subQ2,-1.0]])],"derivedFrom":subQ1}),-1.0]])]});}
            var Q63;
            {var subQ0=sQuery(id+"F1.wireOp",EDGE,"E84");var subQ1=sQuery(id+"F1.wireOp",EDGE,"E12.0");var subQ2=makeQuery(id+"F1.imprint","INTERSECT",VERTEX,{"derivedFrom":[subQ1,subQ0]});Q63=makeQuery(id+"F1.imprint","IMPRINT",FACE,{"disambiguationData":[TD([[makeQuery(id+"F1.imprint","IMPRINT",EDGE,{"disambiguationData":[TD([[subQ2,-1.0]])],"derivedFrom":subQ1}),-1.0]])]});}
            var Q64;
            {var subQ0=sQuery(id+"F1.wireOp",EDGE,"E84");var subQ1=sQuery(id+"F1.wireOp",EDGE,"E26.0");var subQ2=makeQuery(id+"F1.imprint","INTERSECT",VERTEX,{"derivedFrom":[subQ1,subQ0]});Q64=makeQuery(id+"F1.imprint","IMPRINT",FACE,{"disambiguationData":[TD([[makeQuery(id+"F1.imprint","IMPRINT",EDGE,{"disambiguationData":[TD([[subQ2,-1.0]])],"derivedFrom":subQ1}),1.0]])]});}
            var Q65;
            {var subQ0=sQuery(id+"F1.wireOp",EDGE,"E148.trimOffspring");Q65=makeQuery(id+"F1.imprint","IMPRINT",FACE,{"disambiguationData":[TD([[makeQuery(id+"F1.imprint","IMPRINT",EDGE,{"derivedFrom":subQ0}),1.0]])]});}
            var Q66;
            {var subQ0=sQuery(id+"F1.wireOp",EDGE,"E142.trimOffspring");Q66=makeQuery(id+"F1.imprint","IMPRINT",FACE,{"disambiguationData":[TD([[makeQuery(id+"F1.imprint","IMPRINT",EDGE,{"derivedFrom":subQ0}),1.0]])]});}
            var Q67;
            {var subQ0=sQuery(id+"F1.wireOp",EDGE,"E106.trimOffspring");Q67=makeQuery(id+"F1.imprint","IMPRINT",FACE,{"disambiguationData":[TD([[makeQuery(id+"F1.imprint","IMPRINT",EDGE,{"derivedFrom":subQ0}),-1.0]])]});}
            var Q68;
            {var subQ0=sQuery(id+"F1.wireOp",EDGE,"E84");var subQ1=sQuery(id+"F1.wireOp",EDGE,"E28.0");var subQ2=makeQuery(id+"F1.imprint","INTERSECT",VERTEX,{"derivedFrom":[subQ1,subQ0]});Q68=makeQuery(id+"F1.imprint","IMPRINT",FACE,{"disambiguationData":[TD([[makeQuery(id+"F1.imprint","IMPRINT",EDGE,{"disambiguationData":[TD([[subQ2,-1.0]])],"derivedFrom":subQ1}),1.0]])]});}
            var Q69;
            {var subQ0=sQuery(id+"F1.wireOp",EDGE,"E92.trimOffspring");Q69=makeQuery(id+"F1.imprint","IMPRINT",FACE,{"disambiguationData":[TD([[makeQuery(id+"F1.imprint","IMPRINT",EDGE,{"derivedFrom":subQ0}),-1.0]])]});}
            var Q70;
            {var subQ0=sQuery(id+"F1.wireOp",EDGE,"E84");var subQ1=sQuery(id+"F1.wireOp",EDGE,"E7.0");var subQ2=makeQuery(id+"F1.imprint","INTERSECT",VERTEX,{"derivedFrom":[subQ1,subQ0]});Q70=makeQuery(id+"F1.imprint","IMPRINT",FACE,{"disambiguationData":[TD([[makeQuery(id+"F1.imprint","IMPRINT",EDGE,{"disambiguationData":[TD([[subQ2,-1.0]])],"derivedFrom":subQ1}),-1.0]])]});}
            var Q71;
            {var subQ0=sQuery(id+"F1.wireOp",EDGE,"E84");var subQ1=sQuery(id+"F1.wireOp",EDGE,"E31.0");var subQ2=makeQuery(id+"F1.imprint","INTERSECT",VERTEX,{"derivedFrom":[subQ1,subQ0]});Q71=makeQuery(id+"F1.imprint","IMPRINT",FACE,{"disambiguationData":[TD([[makeQuery(id+"F1.imprint","IMPRINT",EDGE,{"disambiguationData":[TD([[subQ2,-1.0]])],"derivedFrom":subQ1}),1.0]])]});}
            var Q72;
            {var subQ0=sQuery(id+"F1.wireOp",EDGE,"E152");Q72=makeQuery(id+"F1.imprint","IMPRINT",FACE,{"disambiguationData":[TD([[makeQuery(id+"F1.imprint","IMPRINT",EDGE,{"derivedFrom":subQ0}),1.0]])]});}
            var Q73;
            {var subQ0=sQuery(id+"F1.wireOp",EDGE,"E87.trimOffspring");Q73=makeQuery(id+"F1.imprint","IMPRINT",FACE,{"disambiguationData":[TD([[makeQuery(id+"F1.imprint","IMPRINT",EDGE,{"derivedFrom":subQ0}),-1.0]])]});}
            var Q74;
            {var subQ0=sQuery(id+"F1.wireOp",EDGE,"E84");var subQ1=sQuery(id+"F1.wireOp",EDGE,"E22.0");var subQ2=makeQuery(id+"F1.imprint","INTERSECT",VERTEX,{"derivedFrom":[subQ1,subQ0]});Q74=makeQuery(id+"F1.imprint","IMPRINT",FACE,{"disambiguationData":[TD([[makeQuery(id+"F1.imprint","IMPRINT",EDGE,{"disambiguationData":[TD([[subQ2,-1.0]])],"derivedFrom":subQ1}),-1.0]])]});}
            var Q75;
            {var subQ0=sQuery(id+"F1.wireOp",EDGE,"E84");var subQ1=sQuery(id+"F1.wireOp",EDGE,"E44.0");var subQ2=makeQuery(id+"F1.imprint","INTERSECT",VERTEX,{"derivedFrom":[subQ1,subQ0]});Q75=makeQuery(id+"F1.imprint","IMPRINT",FACE,{"disambiguationData":[TD([[makeQuery(id+"F1.imprint","IMPRINT",EDGE,{"disambiguationData":[TD([[subQ2,-1.0]])],"derivedFrom":subQ1}),1.0]])]});}
            var Q76;
            {var subQ0=sQuery(id+"F1.wireOp",EDGE,"E84");var subQ1=sQuery(id+"F1.wireOp",EDGE,"E18.0");var subQ2=makeQuery(id+"F1.imprint","INTERSECT",VERTEX,{"derivedFrom":[subQ1,subQ0]});Q76=makeQuery(id+"F1.imprint","IMPRINT",FACE,{"disambiguationData":[TD([[makeQuery(id+"F1.imprint","IMPRINT",EDGE,{"disambiguationData":[TD([[subQ2,-1.0]])],"derivedFrom":subQ1}),1.0]])]});}
            var Q77;
            {var subQ0=sQuery(id+"F1.wireOp",EDGE,"E96.trimOffspring");Q77=makeQuery(id+"F1.imprint","IMPRINT",FACE,{"disambiguationData":[TD([[makeQuery(id+"F1.imprint","IMPRINT",EDGE,{"derivedFrom":subQ0}),-1.0]])]});}
            var Q78;
            {var subQ0=sQuery(id+"F1.wireOp",EDGE,"E139.trimOffspring");Q78=makeQuery(id+"F1.imprint","IMPRINT",FACE,{"disambiguationData":[TD([[makeQuery(id+"F1.imprint","IMPRINT",EDGE,{"derivedFrom":subQ0}),1.0]])]});}
            var Q79;
            {var subQ0=sQuery(id+"F1.wireOp",EDGE,"E84");var subQ1=sQuery(id+"F1.wireOp",EDGE,"E7.0");var subQ2=makeQuery(id+"F1.imprint","INTERSECT",VERTEX,{"derivedFrom":[subQ1,subQ0]});Q79=makeQuery(id+"F1.imprint","IMPRINT",FACE,{"disambiguationData":[TD([[makeQuery(id+"F1.imprint","IMPRINT",EDGE,{"disambiguationData":[TD([[subQ2,-1.0]])],"derivedFrom":subQ1}),1.0]])]});}
            var Q80;
            {var subQ0=sQuery(id+"F1.wireOp",EDGE,"E84");var subQ1=sQuery(id+"F1.wireOp",EDGE,"E30.0");var subQ2=makeQuery(id+"F1.imprint","INTERSECT",VERTEX,{"derivedFrom":[subQ1,subQ0]});Q80=makeQuery(id+"F1.imprint","IMPRINT",FACE,{"disambiguationData":[TD([[makeQuery(id+"F1.imprint","IMPRINT",EDGE,{"disambiguationData":[TD([[subQ2,-1.0]])],"derivedFrom":subQ1}),1.0]])]});}
            var Q81;
            {var subQ0=sQuery(id+"F1.wireOp",EDGE,"E125.trimOffspring");Q81=makeQuery(id+"F1.imprint","IMPRINT",FACE,{"disambiguationData":[TD([[makeQuery(id+"F1.imprint","IMPRINT",EDGE,{"derivedFrom":subQ0}),1.0]])]});}
            var Q82;
            {var subQ0=sQuery(id+"F1.wireOp",EDGE,"E124.trimOffspring");Q82=makeQuery(id+"F1.imprint","IMPRINT",FACE,{"disambiguationData":[TD([[makeQuery(id+"F1.imprint","IMPRINT",EDGE,{"derivedFrom":subQ0}),-1.0]])]});}
            var Q83;
            {var subQ0=sQuery(id+"F1.wireOp",EDGE,"E84");var subQ1=sQuery(id+"F1.wireOp",EDGE,"E27.0");var subQ2=makeQuery(id+"F1.imprint","INTERSECT",VERTEX,{"derivedFrom":[subQ1,subQ0]});Q83=makeQuery(id+"F1.imprint","IMPRINT",FACE,{"disambiguationData":[TD([[makeQuery(id+"F1.imprint","IMPRINT",EDGE,{"disambiguationData":[TD([[subQ2,-1.0]])],"derivedFrom":subQ1}),-1.0]])]});}
            var Q84;
            {var subQ0=sQuery(id+"F1.wireOp",EDGE,"E147.trimOffspring");Q84=makeQuery(id+"F1.imprint","IMPRINT",FACE,{"disambiguationData":[TD([[makeQuery(id+"F1.imprint","IMPRINT",EDGE,{"derivedFrom":subQ0}),1.0]])]});}
            var Q85;
            {var subQ0=sQuery(id+"F1.wireOp",EDGE,"E84");var subQ1=sQuery(id+"F1.wireOp",EDGE,"E37.0");var subQ2=makeQuery(id+"F1.imprint","INTERSECT",VERTEX,{"derivedFrom":[subQ1,subQ0]});Q85=makeQuery(id+"F1.imprint","IMPRINT",FACE,{"disambiguationData":[TD([[makeQuery(id+"F1.imprint","IMPRINT",EDGE,{"disambiguationData":[TD([[subQ2,-1.0]])],"derivedFrom":subQ1}),-1.0]])]});}
            var Q86;
            {var subQ0=sQuery(id+"F1.wireOp",EDGE,"E84");var subQ1=sQuery(id+"F1.wireOp",EDGE,"E32.0");var subQ2=makeQuery(id+"F1.imprint","INTERSECT",VERTEX,{"derivedFrom":[subQ1,subQ0]});Q86=makeQuery(id+"F1.imprint","IMPRINT",FACE,{"disambiguationData":[TD([[makeQuery(id+"F1.imprint","IMPRINT",EDGE,{"disambiguationData":[TD([[subQ2,-1.0]])],"derivedFrom":subQ1}),-1.0]])]});}
            var Q87;
            {var subQ0=sQuery(id+"F1.wireOp",EDGE,"E131");Q87=makeQuery(id+"F1.imprint","IMPRINT",FACE,{"disambiguationData":[TD([[makeQuery(id+"F1.imprint","IMPRINT",EDGE,{"derivedFrom":subQ0}),1.0]])]});}
            var Q88;
            {var subQ0=sQuery(id+"F1.wireOp",EDGE,"E84");var subQ1=sQuery(id+"F1.wireOp",EDGE,"E34.0");var subQ2=makeQuery(id+"F1.imprint","INTERSECT",VERTEX,{"derivedFrom":[subQ1,subQ0]});Q88=makeQuery(id+"F1.imprint","IMPRINT",FACE,{"disambiguationData":[TD([[makeQuery(id+"F1.imprint","IMPRINT",EDGE,{"disambiguationData":[TD([[subQ2,-1.0]])],"derivedFrom":subQ1}),-1.0]])]});}
            var Q89;
            {var subQ0=sQuery(id+"F1.wireOp",EDGE,"E84");var subQ1=sQuery(id+"F1.wireOp",EDGE,"E14.0");var subQ2=makeQuery(id+"F1.imprint","INTERSECT",VERTEX,{"derivedFrom":[subQ1,subQ0]});Q89=makeQuery(id+"F1.imprint","IMPRINT",FACE,{"disambiguationData":[TD([[makeQuery(id+"F1.imprint","IMPRINT",EDGE,{"disambiguationData":[TD([[subQ2,-1.0]])],"derivedFrom":subQ1}),1.0]])]});}
            var Q90;
            {var subQ0=sQuery(id+"F1.wireOp",EDGE,"E145.trimOffspring");Q90=makeQuery(id+"F1.imprint","IMPRINT",FACE,{"disambiguationData":[TD([[makeQuery(id+"F1.imprint","IMPRINT",EDGE,{"derivedFrom":subQ0}),1.0]])]});}
            var Q91;
            {var subQ0=sQuery(id+"F1.wireOp",EDGE,"E84");var subQ1=sQuery(id+"F1.wireOp",EDGE,"E44.0");var subQ2=makeQuery(id+"F1.imprint","INTERSECT",VERTEX,{"derivedFrom":[subQ1,subQ0]});Q91=makeQuery(id+"F1.imprint","IMPRINT",FACE,{"disambiguationData":[TD([[makeQuery(id+"F1.imprint","IMPRINT",EDGE,{"disambiguationData":[TD([[subQ2,-1.0]])],"derivedFrom":subQ1}),-1.0]])]});}
            var Q92;
            {var subQ0=sQuery(id+"F1.wireOp",EDGE,"E101.trimOffspring");Q92=makeQuery(id+"F1.imprint","IMPRINT",FACE,{"disambiguationData":[TD([[makeQuery(id+"F1.imprint","IMPRINT",EDGE,{"derivedFrom":subQ0}),-1.0]])]});}
            var Q93;
            {var subQ0=sQuery(id+"F1.wireOp",EDGE,"E84");var subQ1=sQuery(id+"F1.wireOp",EDGE,"E20.0");var subQ2=makeQuery(id+"F1.imprint","INTERSECT",VERTEX,{"derivedFrom":[subQ1,subQ0]});Q93=makeQuery(id+"F1.imprint","IMPRINT",FACE,{"disambiguationData":[TD([[makeQuery(id+"F1.imprint","IMPRINT",EDGE,{"disambiguationData":[TD([[subQ2,-1.0]])],"derivedFrom":subQ1}),-1.0]])]});}
            var Q94;
            {var subQ0=sQuery(id+"F1.wireOp",EDGE,"E89.trimOffspring");Q94=makeQuery(id+"F1.imprint","IMPRINT",FACE,{"disambiguationData":[TD([[makeQuery(id+"F1.imprint","IMPRINT",EDGE,{"derivedFrom":subQ0}),-1.0]])]});}
            var Q95;
            {var subQ0=sQuery(id+"F1.wireOp",EDGE,"E84");var subQ1=sQuery(id+"F1.wireOp",EDGE,"E36.0");var subQ2=makeQuery(id+"F1.imprint","INTERSECT",VERTEX,{"derivedFrom":[subQ1,subQ0]});Q95=makeQuery(id+"F1.imprint","IMPRINT",FACE,{"disambiguationData":[TD([[makeQuery(id+"F1.imprint","IMPRINT",EDGE,{"disambiguationData":[TD([[subQ2,-1.0]])],"derivedFrom":subQ1}),-1.0]])]});}
            var Q96;
            {var subQ0=sQuery(id+"F1.wireOp",EDGE,"E150.trimOffspring");Q96=makeQuery(id+"F1.imprint","IMPRINT",FACE,{"disambiguationData":[TD([[makeQuery(id+"F1.imprint","IMPRINT",EDGE,{"derivedFrom":subQ0}),1.0]])]});}
            var Q97;
            {var subQ0=sQuery(id+"F1.wireOp",EDGE,"E84");var subQ1=sQuery(id+"F1.wireOp",EDGE,"E34.0");var subQ2=makeQuery(id+"F1.imprint","INTERSECT",VERTEX,{"derivedFrom":[subQ1,subQ0]});Q97=makeQuery(id+"F1.imprint","IMPRINT",FACE,{"disambiguationData":[TD([[makeQuery(id+"F1.imprint","IMPRINT",EDGE,{"disambiguationData":[TD([[subQ2,-1.0]])],"derivedFrom":subQ1}),1.0]])]});}
            var Q98;
            {var subQ0=sQuery(id+"F1.wireOp",EDGE,"E103.trimOffspring");Q98=makeQuery(id+"F1.imprint","IMPRINT",FACE,{"disambiguationData":[TD([[makeQuery(id+"F1.imprint","IMPRINT",EDGE,{"derivedFrom":subQ0}),-1.0]])]});}
            var Q99;
            {var subQ0=sQuery(id+"F1.wireOp",EDGE,"E84");var subQ1=sQuery(id+"F1.wireOp",EDGE,"E16.0");var subQ2=makeQuery(id+"F1.imprint","INTERSECT",VERTEX,{"derivedFrom":[subQ1,subQ0]});Q99=makeQuery(id+"F1.imprint","IMPRINT",FACE,{"disambiguationData":[TD([[makeQuery(id+"F1.imprint","IMPRINT",EDGE,{"disambiguationData":[TD([[subQ2,-1.0]])],"derivedFrom":subQ1}),-1.0]])]});}
            var Q100;
            {var subQ0=sQuery(id+"F1.wireOp",EDGE,"E109.trimOffspring");Q100=makeQuery(id+"F1.imprint","IMPRINT",FACE,{"disambiguationData":[TD([[makeQuery(id+"F1.imprint","IMPRINT",EDGE,{"derivedFrom":subQ0}),-1.0]])]});}
            var Q101;
            {var subQ0=sQuery(id+"F1.wireOp",EDGE,"E155.trimOffspring");Q101=makeQuery(id+"F1.imprint","IMPRINT",FACE,{"disambiguationData":[TD([[makeQuery(id+"F1.imprint","IMPRINT",EDGE,{"derivedFrom":subQ0}),1.0]])]});}
            var Q102;
            {var subQ0=sQuery(id+"F1.wireOp",EDGE,"E90.trimOffspring");Q102=makeQuery(id+"F1.imprint","IMPRINT",FACE,{"disambiguationData":[TD([[makeQuery(id+"F1.imprint","IMPRINT",EDGE,{"derivedFrom":subQ0}),-1.0]])]});}
            var Q103;
            {var subQ0=sQuery(id+"F1.wireOp",EDGE,"E128.trimOffspring");Q103=makeQuery(id+"F1.imprint","IMPRINT",FACE,{"disambiguationData":[TD([[makeQuery(id+"F1.imprint","IMPRINT",EDGE,{"derivedFrom":subQ0}),1.0]])]});}
            var Q104;
            {var subQ0=sQuery(id+"F1.wireOp",EDGE,"E84");var subQ1=sQuery(id+"F1.wireOp",EDGE,"E23.0");var subQ2=makeQuery(id+"F1.imprint","INTERSECT",VERTEX,{"derivedFrom":[subQ1,subQ0]});Q104=makeQuery(id+"F1.imprint","IMPRINT",FACE,{"disambiguationData":[TD([[makeQuery(id+"F1.imprint","IMPRINT",EDGE,{"disambiguationData":[TD([[subQ2,-1.0]])],"derivedFrom":subQ1}),-1.0]])]});}
            var Q105;
            {var subQ0=sQuery(id+"F1.wireOp",EDGE,"E84");var subQ1=sQuery(id+"F1.wireOp",EDGE,"E42.0");var subQ2=makeQuery(id+"F1.imprint","INTERSECT",VERTEX,{"derivedFrom":[subQ1,subQ0]});Q105=makeQuery(id+"F1.imprint","IMPRINT",FACE,{"disambiguationData":[TD([[makeQuery(id+"F1.imprint","IMPRINT",EDGE,{"disambiguationData":[TD([[subQ2,-1.0]])],"derivedFrom":subQ1}),1.0]])]});}
            var Q106;
            {var subQ0=sQuery(id+"F1.wireOp",EDGE,"E108.trimOffspring");Q106=makeQuery(id+"F1.imprint","IMPRINT",FACE,{"disambiguationData":[TD([[makeQuery(id+"F1.imprint","IMPRINT",EDGE,{"derivedFrom":subQ0}),-1.0]])]});}
            var Q107;
            {var subQ0=sQuery(id+"F1.wireOp",EDGE,"E84");var subQ1=sQuery(id+"F1.wireOp",EDGE,"E29.0");var subQ2=makeQuery(id+"F1.imprint","INTERSECT",VERTEX,{"derivedFrom":[subQ1,subQ0]});Q107=makeQuery(id+"F1.imprint","IMPRINT",FACE,{"disambiguationData":[TD([[makeQuery(id+"F1.imprint","IMPRINT",EDGE,{"disambiguationData":[TD([[subQ2,-1.0]])],"derivedFrom":subQ1}),1.0]])]});}
            var Q108;
            {var subQ0=sQuery(id+"F1.wireOp",EDGE,"E110.trimOffspring");Q108=makeQuery(id+"F1.imprint","IMPRINT",FACE,{"disambiguationData":[TD([[makeQuery(id+"F1.imprint","IMPRINT",EDGE,{"derivedFrom":subQ0}),-1.0]])]});}
            var Q109;
            {var subQ0=sQuery(id+"F1.wireOp",EDGE,"E159");Q109=makeQuery(id+"F1.imprint","IMPRINT",FACE,{"disambiguationData":[TD([[makeQuery(id+"F1.imprint","IMPRINT",EDGE,{"derivedFrom":subQ0}),1.0]])]});}
            var Q110;
            {var subQ0=sQuery(id+"F1.wireOp",EDGE,"E119.trimOffspring");Q110=makeQuery(id+"F1.imprint","IMPRINT",FACE,{"disambiguationData":[TD([[makeQuery(id+"F1.imprint","IMPRINT",EDGE,{"derivedFrom":subQ0}),-1.0]])]});}
            var Q111;
            {var subQ0=sQuery(id+"F1.wireOp",EDGE,"E84");var subQ1=sQuery(id+"F1.wireOp",EDGE,"E24.0");var subQ2=makeQuery(id+"F1.imprint","INTERSECT",VERTEX,{"derivedFrom":[subQ1,subQ0]});Q111=makeQuery(id+"F1.imprint","IMPRINT",FACE,{"disambiguationData":[TD([[makeQuery(id+"F1.imprint","IMPRINT",EDGE,{"disambiguationData":[TD([[subQ2,-1.0]])],"derivedFrom":subQ1}),-1.0]])]});}
            var Q112;
            {var subQ0=sQuery(id+"F1.wireOp",EDGE,"E97.trimOffspring");Q112=makeQuery(id+"F1.imprint","IMPRINT",FACE,{"disambiguationData":[TD([[makeQuery(id+"F1.imprint","IMPRINT",EDGE,{"derivedFrom":subQ0}),-1.0]])]});}
            var Q113;
            {var subQ0=sQuery(id+"F1.wireOp",EDGE,"E84");var subQ1=sQuery(id+"F1.wireOp",EDGE,"E23.0");var subQ2=makeQuery(id+"F1.imprint","INTERSECT",VERTEX,{"derivedFrom":[subQ1,subQ0]});Q113=makeQuery(id+"F1.imprint","IMPRINT",FACE,{"disambiguationData":[TD([[makeQuery(id+"F1.imprint","IMPRINT",EDGE,{"disambiguationData":[TD([[subQ2,-1.0]])],"derivedFrom":subQ1}),1.0]])]});}
            var Q114;
            {var subQ0=sQuery(id+"F1.wireOp",EDGE,"E132");Q114=makeQuery(id+"F1.imprint","IMPRINT",FACE,{"disambiguationData":[TD([[makeQuery(id+"F1.imprint","IMPRINT",EDGE,{"derivedFrom":subQ0}),1.0]])]});}
            var Q115;
            {var subQ0=sQuery(id+"F1.wireOp",EDGE,"E84");var subQ1=sQuery(id+"F1.wireOp",EDGE,"E8.0");var subQ2=makeQuery(id+"F1.imprint","INTERSECT",VERTEX,{"derivedFrom":[subQ1,subQ0]});Q115=makeQuery(id+"F1.imprint","IMPRINT",FACE,{"disambiguationData":[TD([[makeQuery(id+"F1.imprint","IMPRINT",EDGE,{"disambiguationData":[TD([[subQ2,-1.0]])],"derivedFrom":subQ1}),1.0]])]});}
            var Q116;
            {var subQ0=sQuery(id+"F1.wireOp",EDGE,"E84");var subQ1=sQuery(id+"F1.wireOp",EDGE,"E16.0");var subQ2=makeQuery(id+"F1.imprint","INTERSECT",VERTEX,{"derivedFrom":[subQ1,subQ0]});Q116=makeQuery(id+"F1.imprint","IMPRINT",FACE,{"disambiguationData":[TD([[makeQuery(id+"F1.imprint","IMPRINT",EDGE,{"disambiguationData":[TD([[subQ2,-1.0]])],"derivedFrom":subQ1}),1.0]])]});}
            var Q117;
            {var subQ0=sQuery(id+"F1.wireOp",EDGE,"E84");var subQ1=sQuery(id+"F1.wireOp",EDGE,"E15.0");var subQ2=makeQuery(id+"F1.imprint","INTERSECT",VERTEX,{"derivedFrom":[subQ1,subQ0]});Q117=makeQuery(id+"F1.imprint","IMPRINT",FACE,{"disambiguationData":[TD([[makeQuery(id+"F1.imprint","IMPRINT",EDGE,{"disambiguationData":[TD([[subQ2,-1.0]])],"derivedFrom":subQ1}),1.0]])]});}
            var Q118;
            {var subQ0=sQuery(id+"F1.wireOp",EDGE,"E84");var subQ1=sQuery(id+"F1.wireOp",EDGE,"E41.0");var subQ2=makeQuery(id+"F1.imprint","INTERSECT",VERTEX,{"derivedFrom":[subQ1,subQ0]});Q118=makeQuery(id+"F1.imprint","IMPRINT",FACE,{"disambiguationData":[TD([[makeQuery(id+"F1.imprint","IMPRINT",EDGE,{"disambiguationData":[TD([[subQ2,-1.0]])],"derivedFrom":subQ1}),-1.0]])]});}
            var Q119;
            {var subQ0=sQuery(id+"F1.wireOp",EDGE,"E157.trimOffspring");Q119=makeQuery(id+"F1.imprint","IMPRINT",FACE,{"disambiguationData":[TD([[makeQuery(id+"F1.imprint","IMPRINT",EDGE,{"derivedFrom":subQ0}),1.0]])]});}
            var Q120;
            {var subQ0=sQuery(id+"F1.wireOp",EDGE,"E84");var subQ1=sQuery(id+"F1.wireOp",EDGE,"E6.0");var subQ2=makeQuery(id+"F1.imprint","INTERSECT",VERTEX,{"derivedFrom":[subQ1,subQ0]});Q120=makeQuery(id+"F1.imprint","IMPRINT",FACE,{"disambiguationData":[TD([[makeQuery(id+"F1.imprint","IMPRINT",EDGE,{"disambiguationData":[TD([[subQ2,-1.0]])],"derivedFrom":subQ1}),1.0]])]});}
            var Q121;
            {var subQ0=sQuery(id+"F1.wireOp",EDGE,"E104.trimOffspring");Q121=makeQuery(id+"F1.imprint","IMPRINT",FACE,{"disambiguationData":[TD([[makeQuery(id+"F1.imprint","IMPRINT",EDGE,{"derivedFrom":subQ0}),-1.0]])]});}
            var Q122;
            {var subQ0=sQuery(id+"F1.wireOp",EDGE,"E94.trimOffspring");Q122=makeQuery(id+"F1.imprint","IMPRINT",FACE,{"disambiguationData":[TD([[makeQuery(id+"F1.imprint","IMPRINT",EDGE,{"derivedFrom":subQ0}),-1.0]])]});}
            var Q123;
            {var subQ0=sQuery(id+"F1.wireOp",EDGE,"E84");var subQ1=sQuery(id+"F1.wireOp",EDGE,"E11.0");var subQ2=makeQuery(id+"F1.imprint","INTERSECT",VERTEX,{"derivedFrom":[subQ1,subQ0]});Q123=makeQuery(id+"F1.imprint","IMPRINT",FACE,{"disambiguationData":[TD([[makeQuery(id+"F1.imprint","IMPRINT",EDGE,{"disambiguationData":[TD([[subQ2,-1.0]])],"derivedFrom":subQ1}),-1.0]])]});}
            var Q124;
            {var subQ0=sQuery(id+"F1.wireOp",EDGE,"E84");var subQ1=sQuery(id+"F1.wireOp",EDGE,"E38.0");var subQ2=makeQuery(id+"F1.imprint","INTERSECT",VERTEX,{"derivedFrom":[subQ1,subQ0]});Q124=makeQuery(id+"F1.imprint","IMPRINT",FACE,{"disambiguationData":[TD([[makeQuery(id+"F1.imprint","IMPRINT",EDGE,{"disambiguationData":[TD([[subQ2,-1.0]])],"derivedFrom":subQ1}),-1.0]])]});}
            var Q125;
            {var subQ0=sQuery(id+"F1.wireOp",EDGE,"E84");var subQ1=sQuery(id+"F1.wireOp",EDGE,"E10.0");var subQ2=makeQuery(id+"F1.imprint","INTERSECT",VERTEX,{"derivedFrom":[subQ1,subQ0]});Q125=makeQuery(id+"F1.imprint","IMPRINT",FACE,{"disambiguationData":[TD([[makeQuery(id+"F1.imprint","IMPRINT",EDGE,{"disambiguationData":[TD([[subQ2,-1.0]])],"derivedFrom":subQ1}),1.0]])]});}
            var Q126;
            {var subQ0=sQuery(id+"F1.wireOp",EDGE,"E111.trimOffspring");Q126=makeQuery(id+"F1.imprint","IMPRINT",FACE,{"disambiguationData":[TD([[makeQuery(id+"F1.imprint","IMPRINT",EDGE,{"derivedFrom":subQ0}),-1.0]])]});}
            var Q127;
            {var subQ0=sQuery(id+"F1.wireOp",EDGE,"E144.trimOffspring");Q127=makeQuery(id+"F1.imprint","IMPRINT",FACE,{"disambiguationData":[TD([[makeQuery(id+"F1.imprint","IMPRINT",EDGE,{"derivedFrom":subQ0}),1.0]])]});}
            var Q128;
            {var subQ0=sQuery(id+"F1.wireOp",EDGE,"E135.trimOffspring");Q128=makeQuery(id+"F1.imprint","IMPRINT",FACE,{"disambiguationData":[TD([[makeQuery(id+"F1.imprint","IMPRINT",EDGE,{"derivedFrom":subQ0}),1.0]])]});}
            var Q129;
            {var subQ0=sQuery(id+"F1.wireOp",EDGE,"E84");var subQ1=sQuery(id+"F1.wireOp",EDGE,"E13.0");var subQ2=makeQuery(id+"F1.imprint","INTERSECT",VERTEX,{"derivedFrom":[subQ1,subQ0]});Q129=makeQuery(id+"F1.imprint","IMPRINT",FACE,{"disambiguationData":[TD([[makeQuery(id+"F1.imprint","IMPRINT",EDGE,{"disambiguationData":[TD([[subQ2,-1.0]])],"derivedFrom":subQ1}),1.0]])]});}
            var Q130;
            {var subQ0=sQuery(id+"F1.wireOp",EDGE,"E84");var subQ1=sQuery(id+"F1.wireOp",EDGE,"E25.0");var subQ2=makeQuery(id+"F1.imprint","INTERSECT",VERTEX,{"derivedFrom":[subQ1,subQ0]});Q130=makeQuery(id+"F1.imprint","IMPRINT",FACE,{"disambiguationData":[TD([[makeQuery(id+"F1.imprint","IMPRINT",EDGE,{"disambiguationData":[TD([[subQ2,-1.0]])],"derivedFrom":subQ1}),1.0]])]});}
            var Q131;
            {var subQ0=sQuery(id+"F1.wireOp",EDGE,"E162");Q131=makeQuery(id+"F1.imprint","IMPRINT",FACE,{"disambiguationData":[TD([[makeQuery(id+"F1.imprint","IMPRINT",EDGE,{"derivedFrom":subQ0}),1.0]])]});}
            var Q132;
            {var subQ0=sQuery(id+"F1.wireOp",EDGE,"E137");Q132=makeQuery(id+"F1.imprint","IMPRINT",FACE,{"disambiguationData":[TD([[makeQuery(id+"F1.imprint","IMPRINT",EDGE,{"derivedFrom":subQ0}),1.0]])]});}
            var Q133;
            {var subQ0=sQuery(id+"F1.wireOp",EDGE,"E116.trimOffspring");Q133=makeQuery(id+"F1.imprint","IMPRINT",FACE,{"disambiguationData":[TD([[makeQuery(id+"F1.imprint","IMPRINT",EDGE,{"derivedFrom":subQ0}),-1.0]])]});}
            var Q134;
            {var subQ0=sQuery(id+"F1.wireOp",EDGE,"E126.trimOffspring");Q134=makeQuery(id+"F1.imprint","IMPRINT",FACE,{"disambiguationData":[TD([[makeQuery(id+"F1.imprint","IMPRINT",EDGE,{"derivedFrom":subQ0}),1.0]])]});}
            var Q135;
            {var subQ0=sQuery(id+"F1.wireOp",EDGE,"E84");var subQ1=sQuery(id+"F1.wireOp",EDGE,"E9.0");var subQ2=makeQuery(id+"F1.imprint","INTERSECT",VERTEX,{"derivedFrom":[subQ1,subQ0]});Q135=makeQuery(id+"F1.imprint","IMPRINT",FACE,{"disambiguationData":[TD([[makeQuery(id+"F1.imprint","IMPRINT",EDGE,{"disambiguationData":[TD([[subQ2,-1.0]])],"derivedFrom":subQ1}),1.0]])]});}
            var Q136;
            {var subQ0=sQuery(id+"F1.wireOp",EDGE,"E84");var subQ1=sQuery(id+"F1.wireOp",EDGE,"E40.0");var subQ2=makeQuery(id+"F1.imprint","INTERSECT",VERTEX,{"derivedFrom":[subQ1,subQ0]});Q136=makeQuery(id+"F1.imprint","IMPRINT",FACE,{"disambiguationData":[TD([[makeQuery(id+"F1.imprint","IMPRINT",EDGE,{"disambiguationData":[TD([[subQ2,-1.0]])],"derivedFrom":subQ1}),-1.0]])]});}
            var Q137;
            {var subQ0=sQuery(id+"F1.wireOp",EDGE,"E149.trimOffspring");Q137=makeQuery(id+"F1.imprint","IMPRINT",FACE,{"disambiguationData":[TD([[makeQuery(id+"F1.imprint","IMPRINT",EDGE,{"derivedFrom":subQ0}),1.0]])]});}
            var Q138;
            {var subQ0=sQuery(id+"F1.wireOp",EDGE,"E84");var subQ1=sQuery(id+"F1.wireOp",EDGE,"E25.0");var subQ2=makeQuery(id+"F1.imprint","INTERSECT",VERTEX,{"derivedFrom":[subQ1,subQ0]});Q138=makeQuery(id+"F1.imprint","IMPRINT",FACE,{"disambiguationData":[TD([[makeQuery(id+"F1.imprint","IMPRINT",EDGE,{"disambiguationData":[TD([[subQ2,-1.0]])],"derivedFrom":subQ1}),-1.0]])]});}
            var Q139;
            {var subQ0=sQuery(id+"F1.wireOp",EDGE,"E84");var subQ1=sQuery(id+"F1.wireOp",EDGE,"E41.0");var subQ2=makeQuery(id+"F1.imprint","INTERSECT",VERTEX,{"derivedFrom":[subQ1,subQ0]});Q139=makeQuery(id+"F1.imprint","IMPRINT",FACE,{"disambiguationData":[TD([[makeQuery(id+"F1.imprint","IMPRINT",EDGE,{"disambiguationData":[TD([[subQ2,-1.0]])],"derivedFrom":subQ1}),1.0]])]});}
            var Q140;
            {var subQ0=sQuery(id+"F1.wireOp",EDGE,"E84");var subQ1=sQuery(id+"F1.wireOp",EDGE,"E45.0");var subQ2=makeQuery(id+"F1.imprint","INTERSECT",VERTEX,{"derivedFrom":[subQ1,subQ0]});Q140=makeQuery(id+"F1.imprint","IMPRINT",FACE,{"disambiguationData":[TD([[makeQuery(id+"F1.imprint","IMPRINT",EDGE,{"disambiguationData":[TD([[subQ2,-1.0]])],"derivedFrom":subQ1}),-1.0]])]});}
            var Q141;
            {var subQ0=sQuery(id+"F1.wireOp",EDGE,"E98.trimOffspring");Q141=makeQuery(id+"F1.imprint","IMPRINT",FACE,{"disambiguationData":[TD([[makeQuery(id+"F1.imprint","IMPRINT",EDGE,{"derivedFrom":subQ0}),-1.0]])]});}
            var Q142;
            {var subQ0=sQuery(id+"F1.wireOp",EDGE,"E163");Q142=makeQuery(id+"F1.imprint","IMPRINT",FACE,{"disambiguationData":[TD([[makeQuery(id+"F1.imprint","IMPRINT",EDGE,{"derivedFrom":subQ0}),1.0]])]});}
            var Q143;
            {var subQ0=sQuery(id+"F1.wireOp",EDGE,"E153");Q143=makeQuery(id+"F1.imprint","IMPRINT",FACE,{"disambiguationData":[TD([[makeQuery(id+"F1.imprint","IMPRINT",EDGE,{"derivedFrom":subQ0}),1.0]])]});}
            var Q144;
            {var subQ0=sQuery(id+"F1.wireOp",EDGE,"E113.trimOffspring");Q144=makeQuery(id+"F1.imprint","IMPRINT",FACE,{"disambiguationData":[TD([[makeQuery(id+"F1.imprint","IMPRINT",EDGE,{"derivedFrom":subQ0}),-1.0]])]});}
            var Q145;
            {var subQ0=sQuery(id+"F1.wireOp",EDGE,"E84");var subQ1=sQuery(id+"F1.wireOp",EDGE,"E22.0");var subQ2=makeQuery(id+"F1.imprint","INTERSECT",VERTEX,{"derivedFrom":[subQ1,subQ0]});Q145=makeQuery(id+"F1.imprint","IMPRINT",FACE,{"disambiguationData":[TD([[makeQuery(id+"F1.imprint","IMPRINT",EDGE,{"disambiguationData":[TD([[subQ2,-1.0]])],"derivedFrom":subQ1}),1.0]])]});}
            var Q146;
            {var subQ0=sQuery(id+"F1.wireOp",EDGE,"E84");var subQ1=sQuery(id+"F1.wireOp",EDGE,"E39.0");var subQ2=makeQuery(id+"F1.imprint","INTERSECT",VERTEX,{"derivedFrom":[subQ1,subQ0]});Q146=makeQuery(id+"F1.imprint","IMPRINT",FACE,{"disambiguationData":[TD([[makeQuery(id+"F1.imprint","IMPRINT",EDGE,{"disambiguationData":[TD([[subQ2,-1.0]])],"derivedFrom":subQ1}),-1.0]])]});}
            var Q147;
            {var subQ0=sQuery(id+"F1.wireOp",EDGE,"E84");var subQ1=sQuery(id+"F1.wireOp",EDGE,"E33.0");var subQ2=makeQuery(id+"F1.imprint","INTERSECT",VERTEX,{"derivedFrom":[subQ1,subQ0]});Q147=makeQuery(id+"F1.imprint","IMPRINT",FACE,{"disambiguationData":[TD([[makeQuery(id+"F1.imprint","IMPRINT",EDGE,{"disambiguationData":[TD([[subQ2,-1.0]])],"derivedFrom":subQ1}),1.0]])]});}
            var Q148;
            {var subQ0=sQuery(id+"F1.wireOp",EDGE,"E84");var subQ1=sQuery(id+"F1.wireOp",EDGE,"E5.0");var subQ2=makeQuery(id+"F1.imprint","INTERSECT",VERTEX,{"derivedFrom":[subQ1,subQ0]});Q148=makeQuery(id+"F1.imprint","IMPRINT",FACE,{"disambiguationData":[TD([[makeQuery(id+"F1.imprint","IMPRINT",EDGE,{"disambiguationData":[TD([[subQ2,-1.0]])],"derivedFrom":subQ1}),1.0]])]});}
            var Q149;
            {var subQ0=sQuery(id+"F1.wireOp",EDGE,"E160");Q149=makeQuery(id+"F1.imprint","IMPRINT",FACE,{"disambiguationData":[TD([[makeQuery(id+"F1.imprint","IMPRINT",EDGE,{"derivedFrom":subQ0}),1.0]])]});}
            var Q150;
            {var subQ0=sQuery(id+"F1.wireOp",EDGE,"E84");var subQ1=sQuery(id+"F1.wireOp",EDGE,"E20.0");var subQ2=makeQuery(id+"F1.imprint","INTERSECT",VERTEX,{"derivedFrom":[subQ1,subQ0]});Q150=makeQuery(id+"F1.imprint","IMPRINT",FACE,{"disambiguationData":[TD([[makeQuery(id+"F1.imprint","IMPRINT",EDGE,{"disambiguationData":[TD([[subQ2,-1.0]])],"derivedFrom":subQ1}),1.0]])]});}
            var Q151;
            {var subQ0=sQuery(id+"F1.wireOp",EDGE,"E114.trimOffspring");Q151=makeQuery(id+"F1.imprint","IMPRINT",FACE,{"disambiguationData":[TD([[makeQuery(id+"F1.imprint","IMPRINT",EDGE,{"derivedFrom":subQ0}),-1.0]])]});}
            var Q152;
            {var subQ0=sQuery(id+"F1.wireOp",EDGE,"E136.trimOffspring");Q152=makeQuery(id+"F1.imprint","IMPRINT",FACE,{"disambiguationData":[TD([[makeQuery(id+"F1.imprint","IMPRINT",EDGE,{"derivedFrom":subQ0}),1.0]])]});}
            var Q153;
            {var subQ0=sQuery(id+"F1.wireOp",EDGE,"E84");var subQ1=sQuery(id+"F1.wireOp",EDGE,"E4");var subQ2=makeQuery(id+"F1.imprint","INTERSECT",VERTEX,{"derivedFrom":[subQ1,subQ0]});Q153=makeQuery(id+"F1.imprint","IMPRINT",FACE,{"disambiguationData":[TD([[makeQuery(id+"F1.imprint","IMPRINT",EDGE,{"disambiguationData":[TD([[subQ2,1.0]])],"derivedFrom":subQ1}),1.0]])]});}
            var Q154;
            {var subQ0=sQuery(id+"F1.wireOp",EDGE,"E84");var subQ1=sQuery(id+"F1.wireOp",EDGE,"E2");var subQ2=makeQuery(id+"F1.imprint","INTERSECT",VERTEX,{"derivedFrom":[subQ1,subQ0]});Q154=makeQuery(id+"F1.imprint","IMPRINT",FACE,{"disambiguationData":[TD([[makeQuery(id+"F1.imprint","IMPRINT",EDGE,{"disambiguationData":[TD([[subQ2,-1.0]])],"derivedFrom":subQ1}),1.0]])]});}
            var Q155;
            {var subQ0=sQuery(id+"F1.wireOp",EDGE,"E3");Q155=makeQuery(id+"F1.imprint","IMPRINT",FACE,{"disambiguationData":[TD([[makeQuery(id+"F1.imprint","IMPRINT",EDGE,{"derivedFrom":subQ0}),1.0]])]});}
            var Q156;
            {var subQ0=sQuery(id+"F1.wireOp",EDGE,"E86.trimOffspring");Q156=makeQuery(id+"F1.imprint","IMPRINT",FACE,{"disambiguationData":[TD([[makeQuery(id+"F1.imprint","IMPRINT",EDGE,{"derivedFrom":subQ0}),-1.0]])]});}
            var Q157;
            {var subQ0=sQuery(id+"F1.wireOp",EDGE,"E156.trimOffspring");Q157=makeQuery(id+"F1.imprint","IMPRINT",FACE,{"disambiguationData":[TD([[makeQuery(id+"F1.imprint","IMPRINT",EDGE,{"derivedFrom":subQ0}),1.0]])]});}
            var Q158;
            {var subQ0=sQuery(id+"F1.wireOp",EDGE,"E1");Q158=makeQuery(id+"F1.imprint","IMPRINT",FACE,{"disambiguationData":[TD([[makeQuery(id+"F1.imprint","IMPRINT",EDGE,{"derivedFrom":subQ0}),-1.0]])]});}
            extrude(context, id + "F2", {"entities" : qUnion([Q0, Q1, Q2, Q3, Q4, Q5, Q6, Q7, Q8, Q9, Q10, Q11, Q12, Q13, Q14, Q15, Q16, Q17, Q18, Q19, Q20, Q21, Q22, Q23, Q24, Q25, Q26, Q27, Q28, Q29, Q30, Q31, Q32, Q33, Q34, Q35, Q36, Q37, Q38, Q39, Q40, Q41, Q42, Q43, Q44, Q45, Q46, Q47, Q48, Q49, Q50, Q51, Q52, Q53, Q54, Q55, Q56, Q57, Q58, Q59, Q60, Q61, Q62, Q63, Q64, Q65, Q66, Q67, Q68, Q69, Q70, Q71, Q72, Q73, Q74, Q75, Q76, Q77, Q78, Q79, Q80, Q81, Q82, Q83, Q84, Q85, Q86, Q87, Q88, Q89, Q90, Q91, Q92, Q93, Q94, Q95, Q96, Q97, Q98, Q99, Q100, Q101, Q102, Q103, Q104, Q105, Q106, Q107, Q108, Q109, Q110, Q111, Q112, Q113, Q114, Q115, Q116, Q117, Q118, Q119, Q120, Q121, Q122, Q123, Q124, Q125, Q126, Q127, Q128, Q129, Q130, Q131, Q132, Q133, Q134, Q135, Q136, Q137, Q138, Q139, Q140, Q141, Q142, Q143, Q144, Q145, Q146, Q147, Q148, Q149, Q150, Q151, Q152, Q153, Q154, Q155, Q156, Q157, Q158]), "depth" : 3416 * mm, "offsetDistance" : 25 * mm});
        }
        {
            var Q0;
            Q0=makeQuery(id+"F2.opExtrude","SWEPT_FACE",FACE,{"disambiguationData":[OSD([sQuery(id+"F1.wireOp",EDGE,"E2")])]});
            var sketch = newSketch(context, id + "F3", { "sketchPlane" : qUnion([Q0])});
            skPoint(sketch, "E164", {"position": v(-4201, 3416) * mm});
            skLineSegment(sketch, "E165", {"start": v(-4201, 3416) * mm, "end": v(-4201, 3416) * mm});
            skLineSegment(sketch, "E166", {"start": v(-4201, 3716) * mm, "end": v(-4201, 3416) * mm});
            skLineSegment(sketch, "E167", {"start": v(-4201, 3416) * mm, "end": v(-3611, 3416) * mm});
            skLineSegment(sketch, "E168", {"start": v(-3611, 3416) * mm, "end": v(-3611, 3716) * mm});
            skLineSegment(sketch, "E169", {"start": v(-3611, 3716) * mm, "end": v(-4201, 3716) * mm});
            skSolve(sketch);
        }
        {
            var Q0;
            Q0=makeQuery(id+"F3.imprint","IMPRINT",FACE,{"disambiguationData":[TD([[makeQuery(id+"F3.imprint","IMPRINT",EDGE,{"derivedFrom":sQuery(id+"F3.wireOp",EDGE,"E166")}),1.0]])]});
            extrude(context, id + "F4", {"entities" : qUnion([Q0]), "operationType" : NewBodyOperationType.ADD, "oppositeDirection" : true, "depth" : 3500 * mm, "offsetDistance" : 25 * mm});
        }
        {
            var Q0;
            Q0=makeQuery(id+"F4.boolean.opBoolean","MERGE",FACE,{"derivedFrom":[makeQuery(id+"F2.opExtrude","SWEPT_FACE",FACE,{"disambiguationData":[OSD([sQuery(id+"F1.wireOp",EDGE,"E2")])]}),makeQuery(id+"F4.opExtrude","CAP_FACE",FACE,{"disambiguationData":[OSD([sQuery(id+"F3.wireOp",EDGE,"E166"),sQuery(id+"F3.wireOp",EDGE,"E167"),sQuery(id+"F3.wireOp",EDGE,"E168"),sQuery(id+"F3.wireOp",EDGE,"E169")])],"isStart":true})]});
            var sketch = newSketch(context, id + "F5", { "sketchPlane" : qUnion([Q0])});
            skLineSegment(sketch, "E170", {"start": v(-4311, 3416) * mm, "end": v(-4311, 3716) * mm});
            skLineSegment(sketch, "E171", {"start": v(-4311, 3716) * mm, "end": v(-4901, 3716) * mm});
            skLineSegment(sketch, "E172", {"start": v(-4901, 3716) * mm, "end": v(-4901, 3416) * mm});
            skLineSegment(sketch, "E173", {"start": v(-4901, 3416) * mm, "end": v(-4311, 3416) * mm});
            skSolve(sketch);
        }
        {
            var Q0;
            Q0=makeQuery(id+"F5.imprint","IMPRINT",FACE,{"disambiguationData":[TD([[makeQuery(id+"F5.imprint","IMPRINT",EDGE,{"derivedFrom":sQuery(id+"F5.wireOp",EDGE,"E170")}),1.0]])]});
            extrude(context, id + "F6", {"entities" : qUnion([Q0]), "operationType" : NewBodyOperationType.ADD, "oppositeDirection" : true, "depth" : 11725 * mm, "offsetDistance" : 25 * mm});
        }
        {
            var Q0;
            Q0=makeQuery(id+"F6.opExtrude","SWEPT_FACE",FACE,{"disambiguationData":[OSD([sQuery(id+"F5.wireOp",EDGE,"E171")])]});
            var sketch = newSketch(context, id + "F7", { "sketchPlane" : qUnion([Q0])});
            skPoint(sketch, "E174", {"position": v(-15701.91, 5543) * mm});
            skLineSegment(sketch, "E175", {"start": v(-15701.91, 5543) * mm, "end": v(-15701.91, 3043) * mm});
            skLineSegment(sketch, "E176", {"start": v(-15701.91, 3043) * mm, "end": v(-14401.91, 3043) * mm});
            skLineSegment(sketch, "E177", {"start": v(-14401.91, 3043) * mm, "end": v(-14401.91, 5543) * mm});
            skLineSegment(sketch, "E178", {"start": v(-14401.91, 5543) * mm, "end": v(-15701.91, 5543) * mm});
            skSolve(sketch);
        }
        {
            var Q0;
            {var subQ0=sQuery(id+"F7.wireOp",EDGE,"E178");Q0=makeQuery(id+"F7.imprint","IMPRINT",FACE,{"disambiguationData":[TD([[makeQuery(id+"F7.imprint","IMPRINT",EDGE,{"derivedFrom":subQ0}),1.0]])]});}
            var Q1;
            {var subQ0=sQuery(id+"F7.wireOp",EDGE,"E176");Q1=makeQuery(id+"F7.imprint","IMPRINT",FACE,{"disambiguationData":[TD([[makeQuery(id+"F7.imprint","IMPRINT",EDGE,{"derivedFrom":subQ0}),1.0]])]});}
            var Q2;
            {var subQ0=sQuery(id+"F7.wireOp",EDGE,"E175");var subQ1=sQuery(id+"F5.wireOp",EDGE,"E171");var subQ2=makeQuery(id+"F6.opExtrude","SWEPT_EDGE",EDGE,{"disambiguationData":[OSD([subQ1,sQuery(id+"F5.wireOp",EDGE,"E172")])]});var subQ3=makeQuery(id+"F7.imprint","INTERSECT",VERTEX,{"derivedFrom":[subQ2,subQ0]});Q2=makeQuery(id+"F7.imprint","IMPRINT",FACE,{"disambiguationData":[TD([[makeQuery(id+"F7.imprint","IMPRINT",EDGE,{"disambiguationData":[TD([[subQ3,-1.0]])],"derivedFrom":subQ0}),1.0]])]});}
            extrude(context, id + "F8", {"entities" : qUnion([Q0, Q1, Q2]), "operationType" : NewBodyOperationType.ADD, "depth" : 800 * mm, "offsetDistance" : 25 * mm});
        }
        {
            var Q0;
            Q0=makeQuery(id+"F8.opExtrude","SWEPT_FACE",FACE,{"disambiguationData":[OSD([sQuery(id+"F7.wireOp",EDGE,"E175")])]});
            var sketch = newSketch(context, id + "F9", { "sketchPlane" : qUnion([Q0])});
            skLineSegment(sketch, "E179", {"start": v(-3611, 3716) * mm, "end": v(-3611, 4066) * mm});
            skLineSegment(sketch, "E180", {"start": v(-3611, 4066) * mm, "end": v(-4201, 4066) * mm});
            skLineSegment(sketch, "E181", {"start": v(-4201, 4066) * mm, "end": v(-4201, 3716) * mm});
            skLineSegment(sketch, "E182", {"start": v(-4201, 3716) * mm, "end": v(-3611, 3716) * mm});
            skSolve(sketch);
        }
        {
            var Q1;
            Q1=makeQuery(id+"F4.opExtrude","CAP_FACE",FACE,{"disambiguationData":[OSD([sQuery(id+"F3.wireOp",EDGE,"E166"),sQuery(id+"F3.wireOp",EDGE,"E167"),sQuery(id+"F3.wireOp",EDGE,"E168"),sQuery(id+"F3.wireOp",EDGE,"E169")])],"isStart":false});
            var Q2;
            Q2=makeQuery(id+"F9.imprint","IMPRINT",FACE,{"disambiguationData":[TD([[makeQuery(id+"F9.imprint","IMPRINT",EDGE,{"derivedFrom":sQuery(id+"F9.wireOp",EDGE,"E179")}),1.0]])]});
            loft(context, id + "F10", {"operationType" : NewBodyOperationType.ADD, "sheetProfilesArray" : [{ "sheetProfileEntities" : qUnion([Q1]) }, { "sheetProfileEntities" : qUnion([Q2]) }]});
        }
        {
            var Q0;
            {var subQ0=sQuery(id+"F3.wireOp",EDGE,"E169");Q0=makeQuery(id+"F10.boolean.opBoolean","MERGE",EDGE,{"derivedFrom":[makeQuery(id+"F4.opExtrude","CAP_EDGE",EDGE,{"disambiguationData":[OSD([subQ0])],"isStart":false}),makeQuery(id+"F10.opLoft","MID_CAP_EDGE",EDGE,{"disambiguationData":[OSD([sQuery(id+"F3.wireOp",EDGE,"E166"),sQuery(id+"F3.wireOp",EDGE,"E168"),subQ0])],"capPos":0.0})]});}
            fillet(context, id + "F11", {"entities" : qUnion([Q0]), "radius" : 200 * mm, "tangentPropagation" : true, "allowEdgeOverflow" : false});
        }
    });
